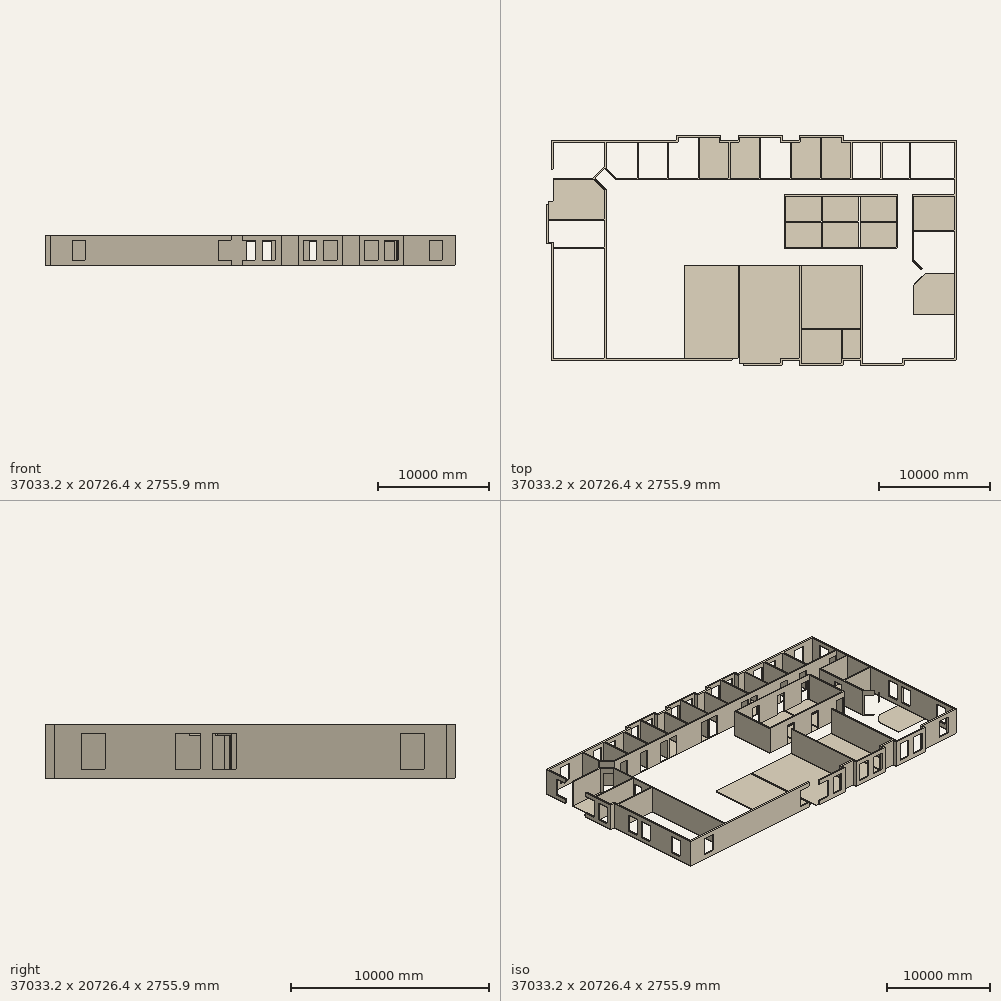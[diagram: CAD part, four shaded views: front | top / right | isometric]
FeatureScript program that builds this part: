
annotation { "Feature Type Name" : "Feature", "Feature Type Description" : "" }
export const myFeature = defineFeature(function(context is Context, id is Id, definition is map)
    precondition{}
    {
        {
            var Q0;
            Q0=qCreatedBy(makeId("Top.planeOp"),FACE);
            var sketch = newSketch(context, id + "F0", { "sketchPlane" : qUnion([Q0])});
            skLineSegment(sketch, "E0", {"start": v(0, 0) * mm, "end": v(11328.4, 0) * mm});
            skLineSegment(sketch, "E1", {"start": v(11328.4, 0) * mm, "end": v(11328.4, 457.2) * mm});
            skLineSegment(sketch, "E2", {"start": v(11328.4, 457.2) * mm, "end": v(15290.8, 457.2) * mm});
            skLineSegment(sketch, "E3", {"start": v(15290.8, 457.2) * mm, "end": v(15290.8, 0) * mm});
            skLineSegment(sketch, "E4", {"start": v(15290.8, 0) * mm, "end": v(16852.9, 0) * mm});
            skLineSegment(sketch, "E5", {"start": v(16852.9, 0) * mm, "end": v(16852.9, 457.2) * mm});
            skLineSegment(sketch, "E6", {"start": v(16852.9, 457.2) * mm, "end": v(20815.3, 457.2) * mm});
            skLineSegment(sketch, "E7", {"start": v(20815.3, 457.2) * mm, "end": v(20815.3, 0) * mm});
            skLineSegment(sketch, "E8", {"start": v(20815.3, 0) * mm, "end": v(22377.4, 0) * mm});
            skLineSegment(sketch, "E9", {"start": v(22377.4, 0) * mm, "end": v(22377.4, 457.2) * mm});
            skLineSegment(sketch, "E10", {"start": v(22377.4, 457.2) * mm, "end": v(26339.8, 457.2) * mm});
            skLineSegment(sketch, "E11", {"start": v(26339.8, 457.2) * mm, "end": v(26339.8, 0) * mm});
            skLineSegment(sketch, "E12", {"start": v(26339.8, 0) * mm, "end": v(36576, 0) * mm});
            skLineSegment(sketch, "E13", {"start": v(0, 0) * mm, "end": v(0, -5330.83) * mm});
            skLineSegment(sketch, "E14", {"start": v(0, -19812) * mm, "end": v(16856.08, -19812) * mm});
            skLineSegment(sketch, "E15", {"start": v(36576, 0) * mm, "end": v(36576, -19812) * mm});
            skLineSegment(sketch, "E16.0", {"start": v(152.4, -152.4) * mm, "end": v(152.4, -5483.23) * mm});
            skLineSegment(sketch, "E16.1", {"start": v(152.4, -19659.6) * mm, "end": v(17008.48, -19659.6) * mm});
            skLineSegment(sketch, "E16.2", {"start": v(36423.6, -152.4) * mm, "end": v(36423.6, -19659.6) * mm});
            skLineSegment(sketch, "E16.3", {"start": v(26187.4, -152.4) * mm, "end": v(36423.6, -152.4) * mm});
            skLineSegment(sketch, "E16.4", {"start": v(26187.4, 304.8) * mm, "end": v(26187.4, -152.4) * mm});
            skLineSegment(sketch, "E16.5", {"start": v(15138.4, -152.4) * mm, "end": v(17005.3, -152.4) * mm});
            skLineSegment(sketch, "E16.6", {"start": v(15138.4, 304.8) * mm, "end": v(15138.4, -152.4) * mm});
            skLineSegment(sketch, "E16.7", {"start": v(11480.8, 304.8) * mm, "end": v(15138.4, 304.8) * mm});
            skLineSegment(sketch, "E16.8", {"start": v(11480.8, -152.4) * mm, "end": v(11480.8, 304.8) * mm});
            skLineSegment(sketch, "E16.9", {"start": v(17005.3, -152.4) * mm, "end": v(17005.3, 304.8) * mm});
            skLineSegment(sketch, "E16.10", {"start": v(17005.3, 304.8) * mm, "end": v(20662.9, 304.8) * mm});
            skLineSegment(sketch, "E16.11", {"start": v(20662.9, 304.8) * mm, "end": v(20662.9, -152.4) * mm});
            skLineSegment(sketch, "E16.12", {"start": v(20662.9, -152.4) * mm, "end": v(22529.8, -152.4) * mm});
            skLineSegment(sketch, "E16.13", {"start": v(22529.8, -152.4) * mm, "end": v(22529.8, 304.8) * mm});
            skLineSegment(sketch, "E16.14", {"start": v(152.4, -152.4) * mm, "end": v(11480.8, -152.4) * mm});
            skLineSegment(sketch, "E16.15", {"start": v(22529.8, 304.8) * mm, "end": v(26187.4, 304.8) * mm});
            skLineSegment(sketch, "E17.bottom", {"start": v(152.4, -3403.6) * mm, "end": v(3762.61, -3403.6) * mm});
            skLineSegment(sketch, "E17.top", {"start": v(152.4, -3517.9) * mm, "end": v(3876.91, -3517.9) * mm});
            skLineSegment(sketch, "E17.left", {"start": v(152.4, -3403.6) * mm, "end": v(152.4, -3517.9) * mm});
            skLineSegment(sketch, "E17.right", {"start": v(36423.6, -3403.6) * mm, "end": v(36423.6, -3517.9) * mm});
            skLineSegment(sketch, "E18", {"start": v(2349.5, 777.7) * mm, "end": v(2349.5, -930.1) * mm, "construction": true});
            skLineSegment(sketch, "E19", {"start": v(6870.7, -930.1) * mm, "end": v(6870.7, 777.7) * mm, "construction": true});
            skLineSegment(sketch, "E20", {"start": v(8699.5, 777.7) * mm, "end": v(8699.5, -930.1) * mm, "construction": true});
            skLineSegment(sketch, "E21", {"start": v(12395.2, 777.7) * mm, "end": v(12395.2, -15.7) * mm, "construction": true});
            skLineSegment(sketch, "E22", {"start": v(14224, -15.7) * mm, "end": v(14224, 777.7) * mm, "construction": true});
            skLineSegment(sketch, "E23", {"start": v(17919.7, 777.7) * mm, "end": v(17919.7, -15.7) * mm, "construction": true});
            skLineSegment(sketch, "E24", {"start": v(19748.5, -15.7) * mm, "end": v(19748.5, 777.7) * mm, "construction": true});
            skLineSegment(sketch, "E25", {"start": v(23444.2, 777.7) * mm, "end": v(23444.2, -15.7) * mm, "construction": true});
            skLineSegment(sketch, "E26", {"start": v(25273, -15.7) * mm, "end": v(25273, 777.7) * mm, "construction": true});
            skLineSegment(sketch, "E27", {"start": v(28895.68, 777.7) * mm, "end": v(28895.68, -930.1) * mm, "construction": true});
            skLineSegment(sketch, "E28", {"start": v(30724.48, -930.1) * mm, "end": v(30724.48, 777.7) * mm, "construction": true});
            skLineSegment(sketch, "E29", {"start": v(34591.63, 777.7) * mm, "end": v(34591.63, -930.1) * mm, "construction": true});
            skPoint(sketch, "E30", {"position": v(8699.5, -76.2) * mm});
            skPoint(sketch, "E31", {"position": v(2349.5, -76.2) * mm});
            skPoint(sketch, "E32", {"position": v(6870.7, -76.2) * mm});
            skPoint(sketch, "E33", {"position": v(28895.68, -76.2) * mm});
            skPoint(sketch, "E34", {"position": v(30724.48, -76.2) * mm});
            skPoint(sketch, "E35", {"position": v(34591.63, -76.2) * mm});
            skPoint(sketch, "E36", {"position": v(23444.2, 381) * mm});
            skPoint(sketch, "E37", {"position": v(25273, 381) * mm});
            skPoint(sketch, "E38", {"position": v(17919.7, 381) * mm});
            skPoint(sketch, "E39", {"position": v(19748.5, 381) * mm});
            skPoint(sketch, "E40", {"position": v(12395.2, 381) * mm});
            skPoint(sketch, "E41", {"position": v(14224, 381) * mm});
            skPoint(sketch, "E42", {"position": v(13309.6, 304.8) * mm});
            skPoint(sketch, "E43", {"position": v(18834.1, 304.8) * mm});
            skPoint(sketch, "E44", {"position": v(24358.6, 304.8) * mm});
            skPoint(sketch, "E45", {"position": v(21596.35, -152.4) * mm});
            skPoint(sketch, "E46", {"position": v(16071.85, -152.4) * mm});
            skPoint(sketch, "E47", {"position": v(29810.08, -152.4) * mm});
            skPoint(sketch, "E48", {"position": v(7785.1, -152.4) * mm});
            skLineSegment(sketch, "E49.bottom", {"start": v(4813.3, -152.4) * mm, "end": v(4927.6, -152.4) * mm});
            skLineSegment(sketch, "E49.left", {"start": v(4813.3, -152.4) * mm, "end": v(4813.3, -2352.91) * mm});
            skLineSegment(sketch, "E49.right", {"start": v(4927.6, -152.4) * mm, "end": v(4927.6, -2467.21) * mm});
            skLineSegment(sketch, "E50.bottom", {"start": v(24301.45, 304.8) * mm, "end": v(24415.75, 304.8) * mm});
            skLineSegment(sketch, "E50.left", {"start": v(24301.45, 304.8) * mm, "end": v(24301.45, -3403.6) * mm});
            skLineSegment(sketch, "E50.right", {"start": v(24415.75, 304.8) * mm, "end": v(24415.75, -3403.6) * mm});
            skLineSegment(sketch, "E51.bottom", {"start": v(18776.95, 304.8) * mm, "end": v(18891.25, 304.8) * mm});
            skLineSegment(sketch, "E51.left", {"start": v(18776.95, 304.8) * mm, "end": v(18776.95, -3403.6) * mm});
            skLineSegment(sketch, "E51.right", {"start": v(18891.25, 304.8) * mm, "end": v(18891.25, -3403.6) * mm});
            skLineSegment(sketch, "E52.bottom", {"start": v(16014.7, -152.4) * mm, "end": v(16129, -152.4) * mm});
            skLineSegment(sketch, "E52.left", {"start": v(16014.7, -152.4) * mm, "end": v(16014.7, -3403.6) * mm});
            skLineSegment(sketch, "E52.right", {"start": v(16129, -152.4) * mm, "end": v(16129, -3403.6) * mm});
            skLineSegment(sketch, "E53.bottom", {"start": v(13252.45, 304.8) * mm, "end": v(13366.75, 304.8) * mm});
            skLineSegment(sketch, "E53.left", {"start": v(13252.45, 304.8) * mm, "end": v(13252.45, -3403.6) * mm});
            skLineSegment(sketch, "E53.right", {"start": v(13366.75, 304.8) * mm, "end": v(13366.75, -3403.6) * mm});
            skLineSegment(sketch, "E54.bottom", {"start": v(7727.95, -152.4) * mm, "end": v(7842.25, -152.4) * mm});
            skLineSegment(sketch, "E54.left", {"start": v(7727.95, -152.4) * mm, "end": v(7727.95, -3403.6) * mm});
            skLineSegment(sketch, "E54.right", {"start": v(7842.25, -152.4) * mm, "end": v(7842.25, -3403.6) * mm});
            skLineSegment(sketch, "E55.bottom", {"start": v(10490.2, -152.4) * mm, "end": v(10604.5, -152.4) * mm});
            skLineSegment(sketch, "E55.left", {"start": v(10490.2, -152.4) * mm, "end": v(10490.2, -3403.6) * mm});
            skLineSegment(sketch, "E55.right", {"start": v(10604.5, -152.4) * mm, "end": v(10604.5, -3403.6) * mm});
            skLineSegment(sketch, "E56.bottom", {"start": v(29752.92, -152.4) * mm, "end": v(29867.23, -152.4) * mm});
            skLineSegment(sketch, "E56.left", {"start": v(29752.92, -152.4) * mm, "end": v(29752.92, -3403.6) * mm});
            skLineSegment(sketch, "E56.right", {"start": v(29867.23, -152.4) * mm, "end": v(29867.23, -3403.6) * mm});
            skLineSegment(sketch, "E57.bottom", {"start": v(21539.2, -152.4) * mm, "end": v(21653.5, -152.4) * mm});
            skLineSegment(sketch, "E57.left", {"start": v(21539.2, -152.4) * mm, "end": v(21539.2, -3403.6) * mm});
            skLineSegment(sketch, "E57.right", {"start": v(21653.5, -152.4) * mm, "end": v(21653.5, -3403.6) * mm});
            skPoint(sketch, "E58", {"position": v(10547.35, -152.4) * mm});
            skPoint(sketch, "E59", {"position": v(27084.34, -152.4) * mm});
            skLineSegment(sketch, "E60.bottom", {"start": v(27027.19, -152.4) * mm, "end": v(27141.49, -152.4) * mm});
            skLineSegment(sketch, "E60.left", {"start": v(27027.19, -152.4) * mm, "end": v(27027.19, -3403.6) * mm});
            skLineSegment(sketch, "E60.right", {"start": v(27141.49, -152.4) * mm, "end": v(27141.49, -3403.6) * mm});
            skLineSegment(sketch, "E61.bottom", {"start": v(11785.6, 457.2) * mm, "end": v(13004.8, 457.2) * mm});
            skLineSegment(sketch, "E61.top", {"start": v(11785.6, 304.8) * mm, "end": v(13004.8, 304.8) * mm});
            skLineSegment(sketch, "E61.left", {"start": v(11785.6, 457.2) * mm, "end": v(11785.6, 304.8) * mm});
            skLineSegment(sketch, "E61.right", {"start": v(13004.8, 457.2) * mm, "end": v(13004.8, 304.8) * mm});
            skLineSegment(sketch, "E62", {"start": v(12395.2, 457.2) * mm, "end": v(12395.2, 304.8) * mm, "construction": true});
            skLineSegment(sketch, "E63.bottom", {"start": v(6261.1, 0) * mm, "end": v(7480.3, 0) * mm});
            skLineSegment(sketch, "E63.top", {"start": v(6261.1, -152.4) * mm, "end": v(7480.3, -152.4) * mm});
            skLineSegment(sketch, "E63.left", {"start": v(6261.1, 0) * mm, "end": v(6261.1, -152.4) * mm});
            skLineSegment(sketch, "E63.right", {"start": v(7480.3, 0) * mm, "end": v(7480.3, -152.4) * mm});
            skLineSegment(sketch, "E64", {"start": v(6870.7, 0) * mm, "end": v(6870.7, -152.4) * mm, "construction": true});
            skLineSegment(sketch, "E65.bottom", {"start": v(8089.9, 0) * mm, "end": v(9309.1, 0) * mm});
            skLineSegment(sketch, "E65.top", {"start": v(8089.9, -152.4) * mm, "end": v(9309.1, -152.4) * mm});
            skLineSegment(sketch, "E65.left", {"start": v(8089.9, 0) * mm, "end": v(8089.9, -152.4) * mm});
            skLineSegment(sketch, "E65.right", {"start": v(9309.1, 0) * mm, "end": v(9309.1, -152.4) * mm});
            skLineSegment(sketch, "E66", {"start": v(8699.5, 0) * mm, "end": v(8699.5, -152.4) * mm, "construction": true});
            skLineSegment(sketch, "E67.bottom", {"start": v(1739.9, 0) * mm, "end": v(2959.1, 0) * mm});
            skLineSegment(sketch, "E67.top", {"start": v(1739.9, -152.4) * mm, "end": v(2959.1, -152.4) * mm});
            skLineSegment(sketch, "E67.left", {"start": v(1739.9, 0) * mm, "end": v(1739.9, -152.4) * mm});
            skLineSegment(sketch, "E67.right", {"start": v(2959.1, 0) * mm, "end": v(2959.1, -152.4) * mm});
            skLineSegment(sketch, "E68", {"start": v(2349.5, 0) * mm, "end": v(2349.5, -152.4) * mm, "construction": true});
            skLineSegment(sketch, "E69.bottom", {"start": v(13614.4, 457.2) * mm, "end": v(14833.6, 457.2) * mm});
            skLineSegment(sketch, "E69.top", {"start": v(13614.4, 304.8) * mm, "end": v(14833.6, 304.8) * mm});
            skLineSegment(sketch, "E69.left", {"start": v(13614.4, 457.2) * mm, "end": v(13614.4, 304.8) * mm});
            skLineSegment(sketch, "E69.right", {"start": v(14833.6, 457.2) * mm, "end": v(14833.6, 304.8) * mm});
            skLineSegment(sketch, "E70", {"start": v(14224, 457.2) * mm, "end": v(14224, 304.8) * mm, "construction": true});
            skLineSegment(sketch, "E71.bottom", {"start": v(17310.1, 457.2) * mm, "end": v(18529.3, 457.2) * mm});
            skLineSegment(sketch, "E71.top", {"start": v(17310.1, 304.8) * mm, "end": v(18529.3, 304.8) * mm});
            skLineSegment(sketch, "E71.left", {"start": v(17310.1, 457.2) * mm, "end": v(17310.1, 304.8) * mm});
            skLineSegment(sketch, "E71.right", {"start": v(18529.3, 457.2) * mm, "end": v(18529.3, 304.8) * mm});
            skLineSegment(sketch, "E72", {"start": v(17919.7, 457.2) * mm, "end": v(17919.7, 304.8) * mm, "construction": true});
            skLineSegment(sketch, "E73.bottom", {"start": v(19138.9, 457.2) * mm, "end": v(20358.1, 457.2) * mm});
            skLineSegment(sketch, "E73.top", {"start": v(19138.9, 304.8) * mm, "end": v(20358.1, 304.8) * mm});
            skLineSegment(sketch, "E73.left", {"start": v(19138.9, 457.2) * mm, "end": v(19138.9, 304.8) * mm});
            skLineSegment(sketch, "E73.right", {"start": v(20358.1, 457.2) * mm, "end": v(20358.1, 304.8) * mm});
            skLineSegment(sketch, "E74", {"start": v(19748.5, 457.2) * mm, "end": v(19748.5, 304.8) * mm, "construction": true});
            skLineSegment(sketch, "E75.bottom", {"start": v(22834.6, 457.2) * mm, "end": v(24053.8, 457.2) * mm});
            skLineSegment(sketch, "E75.top", {"start": v(22834.6, 304.8) * mm, "end": v(24053.8, 304.8) * mm});
            skLineSegment(sketch, "E75.left", {"start": v(22834.6, 457.2) * mm, "end": v(22834.6, 304.8) * mm});
            skLineSegment(sketch, "E75.right", {"start": v(24053.8, 457.2) * mm, "end": v(24053.8, 304.8) * mm});
            skLineSegment(sketch, "E76", {"start": v(23444.2, 457.2) * mm, "end": v(23444.2, 304.8) * mm, "construction": true});
            skLineSegment(sketch, "E77.bottom", {"start": v(24663.4, 457.2) * mm, "end": v(25882.6, 457.2) * mm});
            skLineSegment(sketch, "E77.top", {"start": v(24663.4, 304.8) * mm, "end": v(25882.6, 304.8) * mm});
            skLineSegment(sketch, "E77.left", {"start": v(24663.4, 457.2) * mm, "end": v(24663.4, 304.8) * mm});
            skLineSegment(sketch, "E77.right", {"start": v(25882.6, 457.2) * mm, "end": v(25882.6, 304.8) * mm});
            skLineSegment(sketch, "E78", {"start": v(25273, 457.2) * mm, "end": v(25273, 304.8) * mm, "construction": true});
            skLineSegment(sketch, "E79.bottom", {"start": v(-457.2, -7007.23) * mm, "end": v(-457.2, -5788.03) * mm});
            skLineSegment(sketch, "E79.top", {"start": v(-304.8, -7007.23) * mm, "end": v(-304.8, -5788.03) * mm});
            skLineSegment(sketch, "E79.left", {"start": v(-457.2, -7007.23) * mm, "end": v(-304.8, -7007.23) * mm});
            skLineSegment(sketch, "E79.right", {"start": v(-457.2, -5788.03) * mm, "end": v(-304.8, -5788.03) * mm});
            skLineSegment(sketch, "E80", {"start": v(-457.2, -6397.63) * mm, "end": v(-304.8, -6397.63) * mm, "construction": true});
            skPoint(sketch, "E81", {"position": v(-381, -6397.63) * mm});
            skLineSegment(sketch, "E82.bottom", {"start": v(33982.03, 0) * mm, "end": v(35201.23, 0) * mm});
            skLineSegment(sketch, "E82.top", {"start": v(33982.03, -152.4) * mm, "end": v(35201.23, -152.4) * mm});
            skLineSegment(sketch, "E82.left", {"start": v(33982.03, 0) * mm, "end": v(33982.03, -152.4) * mm});
            skLineSegment(sketch, "E82.right", {"start": v(35201.23, 0) * mm, "end": v(35201.23, -152.4) * mm});
            skLineSegment(sketch, "E83", {"start": v(34591.63, 0) * mm, "end": v(34591.63, -152.4) * mm, "construction": true});
            skLineSegment(sketch, "E84.bottom", {"start": v(30114.88, 0) * mm, "end": v(31334.08, 0) * mm});
            skLineSegment(sketch, "E84.top", {"start": v(30114.87, -152.4) * mm, "end": v(31334.08, -152.4) * mm});
            skLineSegment(sketch, "E84.left", {"start": v(30114.88, 0) * mm, "end": v(30114.88, -152.4) * mm});
            skLineSegment(sketch, "E84.right", {"start": v(31334.08, 0) * mm, "end": v(31334.08, -152.4) * mm});
            skLineSegment(sketch, "E85", {"start": v(30724.48, 0) * mm, "end": v(30724.48, -152.4) * mm, "construction": true});
            skLineSegment(sketch, "E86.bottom", {"start": v(28286.08, 0) * mm, "end": v(29505.28, 0) * mm});
            skLineSegment(sketch, "E86.top", {"start": v(28286.08, -152.4) * mm, "end": v(29505.28, -152.4) * mm});
            skLineSegment(sketch, "E86.left", {"start": v(28286.08, 0) * mm, "end": v(28286.08, -152.4) * mm});
            skLineSegment(sketch, "E86.right", {"start": v(29505.28, 0) * mm, "end": v(29505.28, -152.4) * mm});
            skLineSegment(sketch, "E87", {"start": v(28895.68, 0) * mm, "end": v(28895.68, -152.4) * mm, "construction": true});
            skPoint(sketch, "E88", {"position": v(4870.45, -152.4) * mm});
            skPoint(sketch, "E89", {"position": v(32362.78, -152.4) * mm});
            skLineSegment(sketch, "E90.bottom", {"start": v(32305.63, -152.4) * mm, "end": v(32419.93, -152.4) * mm});
            skLineSegment(sketch, "E90.left", {"start": v(32305.63, -152.4) * mm, "end": v(32305.63, -3403.6) * mm});
            skLineSegment(sketch, "E90.right", {"start": v(32419.93, -152.4) * mm, "end": v(32419.93, -3403.6) * mm});
            skLineSegment(sketch, "E91", {"start": v(4927.6, -4406.95) * mm, "end": v(3924.25, -3403.6) * mm});
            skLineSegment(sketch, "E92", {"start": v(5863.99, -3403.6) * mm, "end": v(4927.6, -2467.21) * mm});
            skLineSegment(sketch, "E93", {"start": v(5816.65, -3517.9) * mm, "end": v(4813.3, -2514.55) * mm});
            skLineSegment(sketch, "E94", {"start": v(4813.3, -4454.29) * mm, "end": v(3876.91, -3517.9) * mm});
            skLineSegment(sketch, "E95", {"start": v(3924.25, -3403.6) * mm, "end": v(4813.3, -2514.55) * mm});
            skLineSegment(sketch, "E96", {"start": v(3762.61, -3403.6) * mm, "end": v(4813.3, -2352.91) * mm});
            skLineSegment(sketch, "E97.trimOffspring", {"start": v(5863.99, -3403.6) * mm, "end": v(36423.6, -3403.6) * mm});
            skLineSegment(sketch, "E98.trimOffspring", {"start": v(5816.65, -3517.9) * mm, "end": v(36423.6, -3517.9) * mm});
            skLineSegment(sketch, "E99.trimOffspring", {"start": v(4813.3, -4454.29) * mm, "end": v(4813.3, -19659.6) * mm});
            skLineSegment(sketch, "E100.trimOffspring", {"start": v(4927.6, -4406.95) * mm, "end": v(4927.6, -19659.6) * mm});
            skLineSegment(sketch, "E101", {"start": v(-1433.95, -6397.63) * mm, "end": v(671.95, -6397.63) * mm, "construction": true});
            skPoint(sketch, "E102", {"position": v(76.2, -1968.5) * mm});
            skLineSegment(sketch, "E103.bottom", {"start": v(0, -14322.43) * mm, "end": v(0, -13103.23) * mm});
            skLineSegment(sketch, "E103.top", {"start": v(152.4, -14322.43) * mm, "end": v(152.4, -13103.23) * mm});
            skLineSegment(sketch, "E103.left", {"start": v(0, -14322.43) * mm, "end": v(152.4, -14322.43) * mm});
            skLineSegment(sketch, "E103.right", {"start": v(0, -13103.23) * mm, "end": v(152.4, -13103.23) * mm});
            skLineSegment(sketch, "E104", {"start": v(0, -13712.83) * mm, "end": v(152.4, -13712.83) * mm, "construction": true});
            skPoint(sketch, "E105", {"position": v(76.2, -13712.83) * mm});
            skLineSegment(sketch, "E106", {"start": v(-603.17, -13712.83) * mm, "end": v(755.57, -13712.83) * mm, "construction": true});
            skLineSegment(sketch, "E107.bottom", {"start": v(0, -12493.63) * mm, "end": v(0, -11274.43) * mm});
            skLineSegment(sketch, "E107.top", {"start": v(152.4, -12493.63) * mm, "end": v(152.4, -11274.43) * mm});
            skLineSegment(sketch, "E107.left", {"start": v(0, -12493.63) * mm, "end": v(152.4, -12493.63) * mm});
            skLineSegment(sketch, "E107.right", {"start": v(0, -11274.43) * mm, "end": v(152.4, -11274.43) * mm});
            skLineSegment(sketch, "E108", {"start": v(0, -11884.03) * mm, "end": v(152.4, -11884.03) * mm, "construction": true});
            skPoint(sketch, "E109", {"position": v(76.2, -11884.03) * mm});
            skLineSegment(sketch, "E110", {"start": v(-593.94, -11884.03) * mm, "end": v(746.34, -11884.03) * mm, "construction": true});
            skLineSegment(sketch, "E111.bottom", {"start": v(0, -2578.1) * mm, "end": v(0, -1358.9) * mm});
            skLineSegment(sketch, "E111.top", {"start": v(152.4, -2578.1) * mm, "end": v(152.4, -1358.9) * mm});
            skLineSegment(sketch, "E111.left", {"start": v(0, -2578.1) * mm, "end": v(152.4, -2578.1) * mm});
            skLineSegment(sketch, "E111.right", {"start": v(0, -1358.9) * mm, "end": v(152.4, -1358.9) * mm});
            skLineSegment(sketch, "E112", {"start": v(0, -1968.5) * mm, "end": v(152.4, -1968.5) * mm, "construction": true});
            skLineSegment(sketch, "E113", {"start": v(-519.55, -1968.5) * mm, "end": v(671.95, -1968.5) * mm, "construction": true});
            skLineSegment(sketch, "E114.bottom", {"start": v(0, -18453.1) * mm, "end": v(0, -17233.9) * mm});
            skLineSegment(sketch, "E114.top", {"start": v(152.4, -18453.1) * mm, "end": v(152.4, -17233.9) * mm});
            skLineSegment(sketch, "E114.left", {"start": v(0, -18453.1) * mm, "end": v(152.4, -18453.1) * mm});
            skLineSegment(sketch, "E114.right", {"start": v(0, -17233.9) * mm, "end": v(152.4, -17233.9) * mm});
            skLineSegment(sketch, "E115", {"start": v(0, -17843.5) * mm, "end": v(152.4, -17843.5) * mm, "construction": true});
            skPoint(sketch, "E116", {"position": v(76.2, -17843.5) * mm});
            skLineSegment(sketch, "E117", {"start": v(-617.62, -17843.5) * mm, "end": v(770.02, -17843.5) * mm, "construction": true});
            skLineSegment(sketch, "E118.bottom", {"start": v(-457.2, -8836.03) * mm, "end": v(-457.2, -7616.83) * mm});
            skLineSegment(sketch, "E118.top", {"start": v(-304.8, -8836.03) * mm, "end": v(-304.8, -7616.83) * mm});
            skLineSegment(sketch, "E118.left", {"start": v(-457.2, -8836.03) * mm, "end": v(-304.8, -8836.03) * mm});
            skLineSegment(sketch, "E118.right", {"start": v(-457.2, -7616.83) * mm, "end": v(-304.8, -7616.83) * mm});
            skLineSegment(sketch, "E119", {"start": v(-457.2, -8226.43) * mm, "end": v(-304.8, -8226.43) * mm, "construction": true});
            skPoint(sketch, "E120", {"position": v(-381, -8226.43) * mm});
            skLineSegment(sketch, "E121", {"start": v(-1375.04, -8226.43) * mm, "end": v(613.04, -8226.43) * mm, "construction": true});
            skLineSegment(sketch, "E122", {"start": v(4813.3, -7064.38) * mm, "end": v(-304.8, -7064.38) * mm});
            skLineSegment(sketch, "E123", {"start": v(-304.8, -7064.38) * mm, "end": v(-304.8, -7178.68) * mm});
            skLineSegment(sketch, "E124", {"start": v(-304.8, -7178.68) * mm, "end": v(4813.3, -7178.68) * mm});
            skLineSegment(sketch, "E125.bottom", {"start": v(-457.2, -5330.83) * mm, "end": v(0, -5330.83) * mm});
            skLineSegment(sketch, "E125.top", {"start": v(-457.2, -9293.23) * mm, "end": v(0, -9293.23) * mm});
            skLineSegment(sketch, "E126.1", {"start": v(-304.8, -5483.23) * mm, "end": v(152.4, -5483.23) * mm});
            skLineSegment(sketch, "E126.3", {"start": v(-304.8, -9140.83) * mm, "end": v(152.4, -9140.83) * mm});
            skLineSegment(sketch, "E127.trimOffspring", {"start": v(0, -9293.23) * mm, "end": v(0, -19812) * mm});
            skLineSegment(sketch, "E128.trimOffspring", {"start": v(152.4, -9140.83) * mm, "end": v(152.4, -19659.6) * mm});
            skLineSegment(sketch, "E129", {"start": v(-457.2, -5330.83) * mm, "end": v(-457.2, -9293.23) * mm});
            skLineSegment(sketch, "E130", {"start": v(-304.8, -5483.23) * mm, "end": v(-304.8, -9140.83) * mm});
            skPoint(sketch, "E131", {"position": v(-304.8, -7121.53) * mm});
            skPoint(sketch, "E132", {"position": v(152.4, -9674.23) * mm});
            skLineSegment(sketch, "E133", {"start": v(4813.3, -9617.08) * mm, "end": v(152.4, -9617.08) * mm});
            skLineSegment(sketch, "E134", {"start": v(152.4, -9617.08) * mm, "end": v(152.4, -9731.38) * mm});
            skLineSegment(sketch, "E135", {"start": v(152.4, -9731.38) * mm, "end": v(4813.3, -9731.38) * mm});
            skLineSegment(sketch, "E136.bottom", {"start": v(32734.25, -5003.8) * mm, "end": v(36423.6, -5003.8) * mm});
            skLineSegment(sketch, "E136.top", {"start": v(32734.25, -8083.55) * mm, "end": v(36423.6, -8083.55) * mm});
            skLineSegment(sketch, "E136.left", {"start": v(32734.25, -5003.8) * mm, "end": v(32734.25, -10845.8) * mm});
            skLineSegment(sketch, "E136.right", {"start": v(36423.6, -5003.8) * mm, "end": v(36423.6, -8083.55) * mm});
            skLineSegment(sketch, "E137.1", {"start": v(32619.95, -4889.5) * mm, "end": v(36423.6, -4889.5) * mm});
            skLineSegment(sketch, "E137.2", {"start": v(32619.95, -4889.5) * mm, "end": v(32619.95, -10893.14) * mm});
            skLineSegment(sketch, "E137.3", {"start": v(32734.25, -8197.85) * mm, "end": v(36423.6, -8197.85) * mm});
            skLineSegment(sketch, "E138.bottom", {"start": v(31248.35, -4889.5) * mm, "end": v(21028.03, -4889.5) * mm});
            skLineSegment(sketch, "E138.top", {"start": v(31248.35, -9747.25) * mm, "end": v(21028.03, -9747.25) * mm});
            skLineSegment(sketch, "E138.left", {"start": v(31248.35, -4889.5) * mm, "end": v(31248.35, -9747.25) * mm});
            skLineSegment(sketch, "E138.right", {"start": v(21028.03, -4889.5) * mm, "end": v(21028.03, -9747.25) * mm});
            skLineSegment(sketch, "E139.0", {"start": v(31134.05, -5003.8) * mm, "end": v(21142.33, -5003.8) * mm});
            skLineSegment(sketch, "E139.1", {"start": v(31134.05, -5003.8) * mm, "end": v(31134.05, -9632.95) * mm});
            skLineSegment(sketch, "E139.2", {"start": v(31134.05, -9632.95) * mm, "end": v(21142.33, -9632.95) * mm});
            skLineSegment(sketch, "E139.3", {"start": v(21142.33, -5003.8) * mm, "end": v(21142.33, -9632.95) * mm});
            skLineSegment(sketch, "E140", {"start": v(21142.33, -7261.23) * mm, "end": v(24396.7, -7261.23) * mm});
            skLineSegment(sketch, "E141", {"start": v(21142.33, -7375.53) * mm, "end": v(24396.7, -7375.53) * mm});
            skLineSegment(sketch, "E142", {"start": v(24396.7, -5003.8) * mm, "end": v(24396.7, -7261.23) * mm});
            skLineSegment(sketch, "E143", {"start": v(24511, -9632.95) * mm, "end": v(24511, -7375.53) * mm});
            skLineSegment(sketch, "E144", {"start": v(27765.38, -5003.8) * mm, "end": v(27765.38, -7261.23) * mm});
            skLineSegment(sketch, "E145", {"start": v(27879.68, -9632.95) * mm, "end": v(27879.68, -7375.53) * mm});
            skLineSegment(sketch, "E146.trimOffspring", {"start": v(24511, -7261.23) * mm, "end": v(27765.38, -7261.23) * mm});
            skLineSegment(sketch, "E147.trimOffspring", {"start": v(24511, -7375.53) * mm, "end": v(27765.38, -7375.53) * mm});
            skLineSegment(sketch, "E148.trimOffspring", {"start": v(24511, -7261.23) * mm, "end": v(24511, -5003.8) * mm});
            skLineSegment(sketch, "E149.trimOffspring", {"start": v(24396.7, -7375.53) * mm, "end": v(24396.7, -9632.95) * mm});
            skLineSegment(sketch, "E150.trimOffspring", {"start": v(27765.38, -7375.53) * mm, "end": v(27765.38, -9632.95) * mm});
            skLineSegment(sketch, "E151.trimOffspring", {"start": v(27879.68, -7261.23) * mm, "end": v(27879.68, -5003.8) * mm});
            skLineSegment(sketch, "E152.trimOffspring", {"start": v(27879.68, -7375.53) * mm, "end": v(31134.05, -7375.53) * mm});
            skLineSegment(sketch, "E153.trimOffspring", {"start": v(27879.68, -7261.23) * mm, "end": v(31134.05, -7261.23) * mm});
            skLineSegment(sketch, "E154.bottom", {"start": v(36423.6, -2336.8) * mm, "end": v(36423.6, -1117.6) * mm});
            skLineSegment(sketch, "E154.top", {"start": v(36576, -2336.8) * mm, "end": v(36576, -1117.6) * mm});
            skLineSegment(sketch, "E154.left", {"start": v(36423.6, -2336.8) * mm, "end": v(36576, -2336.8) * mm});
            skLineSegment(sketch, "E154.right", {"start": v(36423.6, -1117.6) * mm, "end": v(36576, -1117.6) * mm});
            skLineSegment(sketch, "E155", {"start": v(36423.6, -1727.2) * mm, "end": v(36576, -1727.2) * mm, "construction": true});
            skPoint(sketch, "E156", {"position": v(36499.8, -1727.2) * mm});
            skLineSegment(sketch, "E157", {"start": v(35659.18, -1727.2) * mm, "end": v(37340.42, -1727.2) * mm, "construction": true});
            skLineSegment(sketch, "E158.bottom", {"start": v(36423.6, -11849.1) * mm, "end": v(36423.6, -10629.9) * mm});
            skLineSegment(sketch, "E158.top", {"start": v(36576, -11849.1) * mm, "end": v(36576, -10629.9) * mm});
            skLineSegment(sketch, "E158.left", {"start": v(36423.6, -11849.1) * mm, "end": v(36576, -11849.1) * mm});
            skLineSegment(sketch, "E158.right", {"start": v(36423.6, -10629.9) * mm, "end": v(36576, -10629.9) * mm});
            skLineSegment(sketch, "E159", {"start": v(36423.6, -11239.5) * mm, "end": v(36576, -11239.5) * mm, "construction": true});
            skPoint(sketch, "E160", {"position": v(36499.8, -11239.5) * mm});
            skLineSegment(sketch, "E161", {"start": v(35812.04, -11239.5) * mm, "end": v(37187.56, -11239.5) * mm, "construction": true});
            skLineSegment(sketch, "E162.bottom", {"start": v(36423.6, -13677.9) * mm, "end": v(36423.6, -12458.7) * mm});
            skLineSegment(sketch, "E162.top", {"start": v(36576, -13677.9) * mm, "end": v(36576, -12458.7) * mm});
            skLineSegment(sketch, "E162.left", {"start": v(36423.6, -13677.9) * mm, "end": v(36576, -13677.9) * mm});
            skLineSegment(sketch, "E162.right", {"start": v(36423.6, -12458.7) * mm, "end": v(36576, -12458.7) * mm});
            skLineSegment(sketch, "E163", {"start": v(36423.6, -13068.3) * mm, "end": v(36576, -13068.3) * mm, "construction": true});
            skPoint(sketch, "E164", {"position": v(36499.8, -13068.3) * mm});
            skLineSegment(sketch, "E165", {"start": v(35750.9, -13068.3) * mm, "end": v(37248.7, -13068.3) * mm, "construction": true});
            skLineSegment(sketch, "E166.bottom", {"start": v(36423.6, -18453.1) * mm, "end": v(36423.6, -17233.9) * mm});
            skLineSegment(sketch, "E166.top", {"start": v(36576, -18453.1) * mm, "end": v(36576, -17233.9) * mm});
            skLineSegment(sketch, "E166.left", {"start": v(36423.6, -18453.1) * mm, "end": v(36576, -18453.1) * mm});
            skLineSegment(sketch, "E166.right", {"start": v(36423.6, -17233.9) * mm, "end": v(36576, -17233.9) * mm});
            skLineSegment(sketch, "E167", {"start": v(36423.6, -17843.5) * mm, "end": v(36576, -17843.5) * mm, "construction": true});
            skPoint(sketch, "E168", {"position": v(36499.8, -17843.5) * mm});
            skLineSegment(sketch, "E169", {"start": v(35689.76, -17843.5) * mm, "end": v(37309.84, -17843.5) * mm, "construction": true});
            skLineSegment(sketch, "E170", {"start": v(36423.6, -11906.25) * mm, "end": v(36423.6, -12020.55) * mm});
            skLineSegment(sketch, "E171", {"start": v(36423.6, -11849.1) * mm, "end": v(36423.6, -12458.7) * mm});
            skPoint(sketch, "E172", {"position": v(36423.6, -11963.4) * mm});
            skPoint(sketch, "E173", {"position": v(36423.6, -12153.9) * mm});
            skLineSegment(sketch, "E174", {"start": v(30905.92, -11118.85) * mm, "end": v(11918.95, -11118.85) * mm});
            skLineSegment(sketch, "E175", {"start": v(12033.25, -11233.15) * mm, "end": v(16894.18, -11233.15) * mm});
            skLineSegment(sketch, "E176", {"start": v(31867.48, -19812) * mm, "end": v(31867.48, -20269.2) * mm});
            skLineSegment(sketch, "E177", {"start": v(31867.48, -20269.2) * mm, "end": v(27905.08, -20269.2) * mm});
            skLineSegment(sketch, "E178", {"start": v(27905.08, -20269.2) * mm, "end": v(27905.08, -19812) * mm});
            skLineSegment(sketch, "E179", {"start": v(31715.08, -19659.6) * mm, "end": v(31715.08, -20116.8) * mm});
            skLineSegment(sketch, "E180", {"start": v(31715.08, -20116.8) * mm, "end": v(28057.48, -20116.8) * mm});
            skLineSegment(sketch, "E181", {"start": v(28057.48, -20116.8) * mm, "end": v(28057.48, -19659.6) * mm});
            skLineSegment(sketch, "E182", {"start": v(26342.98, -19812) * mm, "end": v(26342.98, -20269.2) * mm});
            skLineSegment(sketch, "E183", {"start": v(26342.98, -20269.2) * mm, "end": v(22380.58, -20269.2) * mm});
            skLineSegment(sketch, "E184", {"start": v(22380.58, -20269.2) * mm, "end": v(22380.58, -19812) * mm});
            skLineSegment(sketch, "E185", {"start": v(26190.58, -19659.6) * mm, "end": v(26190.58, -20116.8) * mm});
            skLineSegment(sketch, "E186", {"start": v(26190.58, -20116.8) * mm, "end": v(22532.98, -20116.8) * mm});
            skLineSegment(sketch, "E187", {"start": v(22532.98, -20116.8) * mm, "end": v(22532.98, -19659.6) * mm});
            skLineSegment(sketch, "E188", {"start": v(20818.48, -19812) * mm, "end": v(20818.48, -20269.2) * mm});
            skLineSegment(sketch, "E189", {"start": v(20818.48, -20269.2) * mm, "end": v(16856.08, -20269.2) * mm});
            skLineSegment(sketch, "E190", {"start": v(16856.08, -20269.2) * mm, "end": v(16856.08, -19812) * mm});
            skLineSegment(sketch, "E191", {"start": v(20666.08, -19659.6) * mm, "end": v(20666.08, -20116.8) * mm});
            skLineSegment(sketch, "E192", {"start": v(20666.08, -20116.8) * mm, "end": v(17008.48, -20116.8) * mm});
            skLineSegment(sketch, "E193", {"start": v(17008.48, -20116.8) * mm, "end": v(17008.48, -19659.6) * mm});
            skLineSegment(sketch, "E194", {"start": v(20818.48, -19812) * mm, "end": v(22380.58, -19812) * mm});
            skLineSegment(sketch, "E195", {"start": v(20666.08, -19659.6) * mm, "end": v(22532.98, -19659.6) * mm});
            skLineSegment(sketch, "E196", {"start": v(26342.98, -19812) * mm, "end": v(27905.08, -19812) * mm});
            skLineSegment(sketch, "E197", {"start": v(26190.58, -19659.6) * mm, "end": v(28057.48, -19659.6) * mm});
            skLineSegment(sketch, "E198", {"start": v(23447.38, -19543.06) * mm, "end": v(23447.38, -20842.94) * mm, "construction": true});
            skLineSegment(sketch, "E199", {"start": v(25276.18, -20842.94) * mm, "end": v(25276.18, -19543.06) * mm, "construction": true});
            skPoint(sketch, "E200", {"position": v(23447.38, -20193) * mm});
            skPoint(sketch, "E201", {"position": v(25276.18, -20193) * mm});
            skLineSegment(sketch, "E202.bottom", {"start": v(22837.78, -20116.8) * mm, "end": v(24056.98, -20116.8) * mm});
            skLineSegment(sketch, "E202.top", {"start": v(22837.78, -20269.2) * mm, "end": v(24056.98, -20269.2) * mm});
            skLineSegment(sketch, "E202.left", {"start": v(22837.78, -20116.8) * mm, "end": v(22837.78, -20269.2) * mm});
            skLineSegment(sketch, "E202.right", {"start": v(24056.98, -20116.8) * mm, "end": v(24056.98, -20269.2) * mm});
            skLineSegment(sketch, "E203", {"start": v(23447.38, -20116.8) * mm, "end": v(23447.38, -20269.2) * mm, "construction": true});
            skLineSegment(sketch, "E204.bottom", {"start": v(24666.58, -20116.8) * mm, "end": v(25885.78, -20116.8) * mm});
            skLineSegment(sketch, "E204.top", {"start": v(24666.58, -20269.2) * mm, "end": v(25885.78, -20269.2) * mm});
            skLineSegment(sketch, "E204.left", {"start": v(24666.58, -20116.8) * mm, "end": v(24666.58, -20269.2) * mm});
            skLineSegment(sketch, "E204.right", {"start": v(25885.78, -20116.8) * mm, "end": v(25885.78, -20269.2) * mm});
            skLineSegment(sketch, "E205", {"start": v(25276.18, -20116.8) * mm, "end": v(25276.18, -20269.2) * mm, "construction": true});
            skPoint(sketch, "E206", {"position": v(24361.78, -20193) * mm});
            skPoint(sketch, "E207", {"position": v(29886.28, -20193) * mm});
            skPoint(sketch, "E208", {"position": v(18837.28, -20193) * mm});
            skLineSegment(sketch, "E209", {"start": v(17922.88, -19558.35) * mm, "end": v(17922.88, -20827.65) * mm, "construction": true});
            skLineSegment(sketch, "E210", {"start": v(19751.68, -20827.65) * mm, "end": v(19751.68, -19558.35) * mm, "construction": true});
            skPoint(sketch, "E211", {"position": v(17922.88, -20193) * mm});
            skPoint(sketch, "E212", {"position": v(19751.68, -20193) * mm});
            skLineSegment(sketch, "E213.bottom", {"start": v(17313.28, -20116.8) * mm, "end": v(18532.48, -20116.8) * mm});
            skLineSegment(sketch, "E213.top", {"start": v(17313.28, -20269.2) * mm, "end": v(18532.48, -20269.2) * mm});
            skLineSegment(sketch, "E213.left", {"start": v(17313.28, -20116.8) * mm, "end": v(17313.28, -20269.2) * mm});
            skLineSegment(sketch, "E213.right", {"start": v(18532.48, -20116.8) * mm, "end": v(18532.48, -20269.2) * mm});
            skLineSegment(sketch, "E214", {"start": v(17922.88, -20116.8) * mm, "end": v(17922.88, -20269.2) * mm, "construction": true});
            skLineSegment(sketch, "E215.bottom", {"start": v(19142.08, -20116.8) * mm, "end": v(20361.28, -20116.8) * mm});
            skLineSegment(sketch, "E215.top", {"start": v(19142.08, -20269.2) * mm, "end": v(20361.28, -20269.2) * mm});
            skLineSegment(sketch, "E215.left", {"start": v(19142.08, -20116.8) * mm, "end": v(19142.08, -20269.2) * mm});
            skLineSegment(sketch, "E215.right", {"start": v(20361.28, -20116.8) * mm, "end": v(20361.28, -20269.2) * mm});
            skLineSegment(sketch, "E216", {"start": v(19751.68, -20116.8) * mm, "end": v(19751.68, -20269.2) * mm, "construction": true});
            skLineSegment(sketch, "E217", {"start": v(28971.88, -19344.36) * mm, "end": v(28971.88, -21041.64) * mm, "construction": true});
            skLineSegment(sketch, "E218", {"start": v(30800.68, -21041.64) * mm, "end": v(30800.68, -19344.36) * mm, "construction": true});
            skPoint(sketch, "E219", {"position": v(28971.88, -20193) * mm});
            skPoint(sketch, "E220", {"position": v(30800.68, -20193) * mm});
            skLineSegment(sketch, "E221.bottom", {"start": v(28362.28, -20116.8) * mm, "end": v(29581.48, -20116.8) * mm});
            skLineSegment(sketch, "E221.top", {"start": v(28362.28, -20269.2) * mm, "end": v(29581.48, -20269.2) * mm});
            skLineSegment(sketch, "E221.left", {"start": v(28362.28, -20116.8) * mm, "end": v(28362.28, -20269.2) * mm});
            skLineSegment(sketch, "E221.right", {"start": v(29581.48, -20116.8) * mm, "end": v(29581.48, -20269.2) * mm});
            skLineSegment(sketch, "E222", {"start": v(28971.88, -20116.8) * mm, "end": v(28971.88, -20269.2) * mm, "construction": true});
            skLineSegment(sketch, "E223.bottom", {"start": v(30191.08, -20116.8) * mm, "end": v(31410.28, -20116.8) * mm});
            skLineSegment(sketch, "E223.top", {"start": v(30191.08, -20269.2) * mm, "end": v(31410.28, -20269.2) * mm});
            skLineSegment(sketch, "E223.left", {"start": v(30191.08, -20116.8) * mm, "end": v(30191.08, -20269.2) * mm});
            skLineSegment(sketch, "E223.right", {"start": v(31410.28, -20116.8) * mm, "end": v(31410.28, -20269.2) * mm});
            skLineSegment(sketch, "E224", {"start": v(30800.68, -20116.8) * mm, "end": v(30800.68, -20269.2) * mm, "construction": true});
            skLineSegment(sketch, "E225.trimOffspring", {"start": v(31867.48, -19812) * mm, "end": v(36576, -19812) * mm});
            skLineSegment(sketch, "E226.trimOffspring", {"start": v(31715.08, -19659.6) * mm, "end": v(36423.6, -19659.6) * mm});
            skPoint(sketch, "E227", {"position": v(34810.7, -19735.8) * mm});
            skLineSegment(sketch, "E228.bottom", {"start": v(34201.1, -19659.6) * mm, "end": v(35420.3, -19659.6) * mm});
            skLineSegment(sketch, "E228.top", {"start": v(34201.1, -19812) * mm, "end": v(35420.3, -19812) * mm});
            skLineSegment(sketch, "E228.left", {"start": v(34201.1, -19659.6) * mm, "end": v(34201.1, -19812) * mm});
            skLineSegment(sketch, "E228.right", {"start": v(35420.3, -19659.6) * mm, "end": v(35420.3, -19812) * mm});
            skLineSegment(sketch, "E229", {"start": v(34810.7, -19659.6) * mm, "end": v(34810.7, -19812) * mm, "construction": true});
            skPoint(sketch, "E230", {"position": v(15738.48, -19735.8) * mm});
            skLineSegment(sketch, "E231.bottom", {"start": v(15128.88, -19659.6) * mm, "end": v(16348.08, -19659.6) * mm});
            skLineSegment(sketch, "E231.top", {"start": v(15128.87, -19812) * mm, "end": v(16348.08, -19812) * mm});
            skLineSegment(sketch, "E231.left", {"start": v(15128.87, -19659.6) * mm, "end": v(15128.87, -19812) * mm});
            skLineSegment(sketch, "E231.right", {"start": v(16348.08, -19659.6) * mm, "end": v(16348.08, -19812) * mm});
            skLineSegment(sketch, "E232", {"start": v(15738.48, -19659.6) * mm, "end": v(15738.48, -19812) * mm, "construction": true});
            skPoint(sketch, "E233", {"position": v(2578.1, -19735.8) * mm});
            skLineSegment(sketch, "E234.bottom", {"start": v(1968.5, -19659.6) * mm, "end": v(3187.7, -19659.6) * mm});
            skLineSegment(sketch, "E234.top", {"start": v(1968.5, -19812) * mm, "end": v(3187.7, -19812) * mm});
            skLineSegment(sketch, "E234.left", {"start": v(1968.5, -19659.6) * mm, "end": v(1968.5, -19812) * mm});
            skLineSegment(sketch, "E234.right", {"start": v(3187.7, -19659.6) * mm, "end": v(3187.7, -19812) * mm});
            skLineSegment(sketch, "E235", {"start": v(2578.1, -19659.6) * mm, "end": v(2578.1, -19812) * mm, "construction": true});
            skLineSegment(sketch, "E236", {"start": v(22532.98, -19659.6) * mm, "end": v(22532.98, -11233.15) * mm});
            skLineSegment(sketch, "E237", {"start": v(28057.48, -19659.6) * mm, "end": v(28057.48, -11233.15) * mm});
            skLineSegment(sketch, "E238", {"start": v(17008.48, -19659.6) * mm, "end": v(17008.48, -11233.15) * mm});
            skLineSegment(sketch, "E239", {"start": v(16894.18, -11233.15) * mm, "end": v(16894.18, -19659.6) * mm});
            skLineSegment(sketch, "E240", {"start": v(22418.68, -11233.15) * mm, "end": v(22418.68, -19659.6) * mm});
            skLineSegment(sketch, "E241", {"start": v(27943.18, -11233.15) * mm, "end": v(27943.18, -19659.6) * mm});
            skLineSegment(sketch, "E242", {"start": v(30858.58, -11233.15) * mm, "end": v(32619.95, -12994.52) * mm});
            skLineSegment(sketch, "E243", {"start": v(32734.25, -13108.82) * mm, "end": v(33822.52, -12020.55) * mm});
            skLineSegment(sketch, "E244", {"start": v(33794.7, -11906.25) * mm, "end": v(32734.25, -10845.8) * mm});
            skLineSegment(sketch, "E245", {"start": v(32619.95, -10893.14) * mm, "end": v(33704.12, -11977.31) * mm});
            skLineSegment(sketch, "E246", {"start": v(33704.12, -11977.31) * mm, "end": v(32734.25, -12947.18) * mm});
            skLineSegment(sketch, "E247", {"start": v(32734.25, -12947.18) * mm, "end": v(30905.92, -11118.85) * mm});
            skLineSegment(sketch, "E248.trimOffspring", {"start": v(33822.52, -12020.55) * mm, "end": v(36423.6, -12020.55) * mm});
            skLineSegment(sketch, "E249.trimOffspring", {"start": v(33794.7, -11906.25) * mm, "end": v(36423.6, -11906.25) * mm});
            skLineSegment(sketch, "E250", {"start": v(32734.25, -13108.82) * mm, "end": v(32734.25, -15728.95) * mm});
            skLineSegment(sketch, "E251", {"start": v(32619.95, -12994.52) * mm, "end": v(32619.95, -15843.25) * mm});
            skLineSegment(sketch, "E252", {"start": v(36423.6, -15728.95) * mm, "end": v(32734.25, -15728.95) * mm});
            skLineSegment(sketch, "E253", {"start": v(36423.6, -15843.25) * mm, "end": v(32619.95, -15843.25) * mm});
            skLineSegment(sketch, "E254", {"start": v(26190.58, -19659.6) * mm, "end": v(26190.58, -17068.8) * mm});
            skLineSegment(sketch, "E255", {"start": v(22418.68, -17068.8) * mm, "end": v(26190.58, -17068.8) * mm});
            skLineSegment(sketch, "E256", {"start": v(22532.98, -16954.5) * mm, "end": v(26304.88, -16954.5) * mm});
            skLineSegment(sketch, "E257", {"start": v(26304.88, -17068.8) * mm, "end": v(26304.88, -19659.6) * mm});
            skLineSegment(sketch, "E258", {"start": v(26304.88, -16954.5) * mm, "end": v(27943.18, -16954.5) * mm});
            skLineSegment(sketch, "E259", {"start": v(26304.88, -17068.8) * mm, "end": v(27943.18, -17068.8) * mm});
            skLineSegment(sketch, "E260", {"start": v(11918.95, -19659.6) * mm, "end": v(11918.95, -11118.85) * mm});
            skLineSegment(sketch, "E261", {"start": v(12033.25, -19659.6) * mm, "end": v(12033.25, -11233.15) * mm});
            skLineSegment(sketch, "E262.trimOffspring", {"start": v(17008.48, -11233.15) * mm, "end": v(30858.58, -11233.15) * mm});
            skLineSegment(sketch, "E263.bottom", {"start": v(6686.55, -3403.6) * mm, "end": v(7651.75, -3403.6) * mm});
            skLineSegment(sketch, "E263.top", {"start": v(6686.55, -3517.9) * mm, "end": v(7651.75, -3517.9) * mm});
            skLineSegment(sketch, "E263.left", {"start": v(6686.55, -3403.6) * mm, "end": v(6686.55, -3517.9) * mm});
            skLineSegment(sketch, "E263.right", {"start": v(7651.75, -3403.6) * mm, "end": v(7651.75, -3517.9) * mm});
            skLineSegment(sketch, "E264.bottom", {"start": v(9448.8, -3403.6) * mm, "end": v(10414, -3403.6) * mm});
            skLineSegment(sketch, "E264.top", {"start": v(9448.8, -3517.9) * mm, "end": v(10414, -3517.9) * mm});
            skLineSegment(sketch, "E264.left", {"start": v(9448.8, -3403.6) * mm, "end": v(9448.8, -3517.9) * mm});
            skLineSegment(sketch, "E264.right", {"start": v(10414, -3403.6) * mm, "end": v(10414, -3517.9) * mm});
            skLineSegment(sketch, "E265.bottom", {"start": v(12211.05, -3403.6) * mm, "end": v(13176.25, -3403.6) * mm});
            skLineSegment(sketch, "E265.top", {"start": v(12211.05, -3517.9) * mm, "end": v(13176.25, -3517.9) * mm});
            skLineSegment(sketch, "E265.left", {"start": v(12211.05, -3403.6) * mm, "end": v(12211.05, -3517.9) * mm});
            skLineSegment(sketch, "E265.right", {"start": v(13176.25, -3403.6) * mm, "end": v(13176.25, -3517.9) * mm});
            skLineSegment(sketch, "E266.bottom", {"start": v(23260.05, -3403.6) * mm, "end": v(24225.25, -3403.6) * mm});
            skLineSegment(sketch, "E266.top", {"start": v(23260.05, -3517.9) * mm, "end": v(24225.25, -3517.9) * mm});
            skLineSegment(sketch, "E266.left", {"start": v(23260.05, -3403.6) * mm, "end": v(23260.05, -3517.9) * mm});
            skLineSegment(sketch, "E266.right", {"start": v(24225.25, -3403.6) * mm, "end": v(24225.25, -3517.9) * mm});
            skLineSegment(sketch, "E267.bottom", {"start": v(17735.55, -3403.6) * mm, "end": v(18700.75, -3403.6) * mm});
            skLineSegment(sketch, "E267.top", {"start": v(17735.55, -3517.9) * mm, "end": v(18700.75, -3517.9) * mm});
            skLineSegment(sketch, "E267.left", {"start": v(17735.55, -3403.6) * mm, "end": v(17735.55, -3517.9) * mm});
            skLineSegment(sketch, "E267.right", {"start": v(18700.75, -3403.6) * mm, "end": v(18700.75, -3517.9) * mm});
            skLineSegment(sketch, "E268.bottom", {"start": v(18967.45, -3403.6) * mm, "end": v(19932.65, -3403.6) * mm});
            skLineSegment(sketch, "E268.top", {"start": v(18967.45, -3517.9) * mm, "end": v(19932.65, -3517.9) * mm});
            skLineSegment(sketch, "E268.left", {"start": v(18967.45, -3403.6) * mm, "end": v(18967.45, -3517.9) * mm});
            skLineSegment(sketch, "E268.right", {"start": v(19932.65, -3403.6) * mm, "end": v(19932.65, -3517.9) * mm});
            skLineSegment(sketch, "E269.bottom", {"start": v(13442.95, -3403.6) * mm, "end": v(14408.15, -3403.6) * mm});
            skLineSegment(sketch, "E269.top", {"start": v(13442.95, -3517.9) * mm, "end": v(14408.15, -3517.9) * mm});
            skLineSegment(sketch, "E269.left", {"start": v(13442.95, -3403.6) * mm, "end": v(13442.95, -3517.9) * mm});
            skLineSegment(sketch, "E269.right", {"start": v(14408.15, -3403.6) * mm, "end": v(14408.15, -3517.9) * mm});
            skLineSegment(sketch, "E270.bottom", {"start": v(35382.2, -3403.6) * mm, "end": v(36347.4, -3403.6) * mm});
            skLineSegment(sketch, "E270.top", {"start": v(35382.2, -3517.9) * mm, "end": v(36347.4, -3517.9) * mm});
            skLineSegment(sketch, "E270.left", {"start": v(35382.2, -3403.6) * mm, "end": v(35382.2, -3517.9) * mm});
            skLineSegment(sketch, "E270.right", {"start": v(36347.4, -3403.6) * mm, "end": v(36347.4, -3517.9) * mm});
            skLineSegment(sketch, "E271.bottom", {"start": v(31264.22, -3403.6) * mm, "end": v(32229.42, -3403.6) * mm});
            skLineSegment(sketch, "E271.top", {"start": v(31264.22, -3517.9) * mm, "end": v(32229.42, -3517.9) * mm});
            skLineSegment(sketch, "E271.left", {"start": v(31264.22, -3403.6) * mm, "end": v(31264.22, -3517.9) * mm});
            skLineSegment(sketch, "E271.right", {"start": v(32229.42, -3403.6) * mm, "end": v(32229.42, -3517.9) * mm});
            skLineSegment(sketch, "E272.bottom", {"start": v(28711.52, -3403.6) * mm, "end": v(29676.72, -3403.6) * mm});
            skLineSegment(sketch, "E272.top", {"start": v(28711.52, -3517.9) * mm, "end": v(29676.72, -3517.9) * mm});
            skLineSegment(sketch, "E272.left", {"start": v(28711.52, -3403.6) * mm, "end": v(28711.52, -3517.9) * mm});
            skLineSegment(sketch, "E272.right", {"start": v(29676.72, -3403.6) * mm, "end": v(29676.72, -3517.9) * mm});
            skLineSegment(sketch, "E273.bottom", {"start": v(24491.95, -3403.6) * mm, "end": v(25457.15, -3403.6) * mm});
            skLineSegment(sketch, "E273.top", {"start": v(24491.95, -3517.9) * mm, "end": v(25457.15, -3517.9) * mm});
            skLineSegment(sketch, "E273.left", {"start": v(24491.95, -3403.6) * mm, "end": v(24491.95, -3517.9) * mm});
            skLineSegment(sketch, "E273.right", {"start": v(25457.15, -3403.6) * mm, "end": v(25457.15, -3517.9) * mm});
            skLineSegment(sketch, "E274.bottom", {"start": v(32619.95, -7042.15) * mm, "end": v(32734.25, -7042.15) * mm});
            skLineSegment(sketch, "E274.top", {"start": v(32619.95, -8007.35) * mm, "end": v(32734.25, -8007.35) * mm});
            skLineSegment(sketch, "E274.left", {"start": v(32619.95, -7042.15) * mm, "end": v(32619.95, -8007.35) * mm});
            skLineSegment(sketch, "E274.right", {"start": v(32734.25, -7042.15) * mm, "end": v(32734.25, -8007.35) * mm});
            skLineSegment(sketch, "E275.bottom", {"start": v(30092.65, -9632.95) * mm, "end": v(31057.85, -9632.95) * mm});
            skLineSegment(sketch, "E275.top", {"start": v(30092.65, -9747.25) * mm, "end": v(31057.85, -9747.25) * mm});
            skLineSegment(sketch, "E275.left", {"start": v(30092.65, -9632.95) * mm, "end": v(30092.65, -9747.25) * mm});
            skLineSegment(sketch, "E275.right", {"start": v(31057.85, -9632.95) * mm, "end": v(31057.85, -9747.25) * mm});
            skLineSegment(sketch, "E276.bottom", {"start": v(26723.98, -9632.95) * mm, "end": v(27689.18, -9632.95) * mm});
            skLineSegment(sketch, "E276.top", {"start": v(26723.98, -9747.25) * mm, "end": v(27689.18, -9747.25) * mm});
            skLineSegment(sketch, "E276.left", {"start": v(26723.98, -9632.95) * mm, "end": v(26723.98, -9747.25) * mm});
            skLineSegment(sketch, "E276.right", {"start": v(27689.18, -9632.95) * mm, "end": v(27689.18, -9747.25) * mm});
            skLineSegment(sketch, "E277.bottom", {"start": v(23355.3, -9632.95) * mm, "end": v(24320.5, -9632.95) * mm});
            skLineSegment(sketch, "E277.top", {"start": v(23355.3, -9747.25) * mm, "end": v(24320.5, -9747.25) * mm});
            skLineSegment(sketch, "E277.left", {"start": v(23355.3, -9632.95) * mm, "end": v(23355.3, -9747.25) * mm});
            skLineSegment(sketch, "E277.right", {"start": v(24320.5, -9632.95) * mm, "end": v(24320.5, -9747.25) * mm});
            skLineSegment(sketch, "E278.bottom", {"start": v(4813.3, -7254.88) * mm, "end": v(4927.6, -7254.88) * mm});
            skLineSegment(sketch, "E278.top", {"start": v(4813.3, -8220.08) * mm, "end": v(4927.6, -8220.08) * mm});
            skLineSegment(sketch, "E278.left", {"start": v(4813.3, -7254.88) * mm, "end": v(4813.3, -8220.08) * mm});
            skLineSegment(sketch, "E278.right", {"start": v(4927.6, -7254.88) * mm, "end": v(4927.6, -8220.08) * mm});
            skLineSegment(sketch, "E279.bottom", {"start": v(23355.3, -4889.5) * mm, "end": v(24320.5, -4889.5) * mm});
            skLineSegment(sketch, "E279.top", {"start": v(23355.3, -5003.8) * mm, "end": v(24320.5, -5003.8) * mm});
            skLineSegment(sketch, "E279.left", {"start": v(23355.3, -4889.5) * mm, "end": v(23355.3, -5003.8) * mm});
            skLineSegment(sketch, "E279.right", {"start": v(24320.5, -4889.5) * mm, "end": v(24320.5, -5003.8) * mm});
            skLineSegment(sketch, "E280.bottom", {"start": v(26723.98, -4889.5) * mm, "end": v(27689.18, -4889.5) * mm});
            skLineSegment(sketch, "E280.top", {"start": v(26723.98, -5003.8) * mm, "end": v(27689.18, -5003.8) * mm});
            skLineSegment(sketch, "E280.left", {"start": v(26723.98, -4889.5) * mm, "end": v(26723.98, -5003.8) * mm});
            skLineSegment(sketch, "E280.right", {"start": v(27689.18, -4889.5) * mm, "end": v(27689.18, -5003.8) * mm});
            skLineSegment(sketch, "E281.bottom", {"start": v(30092.65, -4889.5) * mm, "end": v(31057.85, -4889.5) * mm});
            skLineSegment(sketch, "E281.top", {"start": v(30092.65, -5003.8) * mm, "end": v(31057.85, -5003.8) * mm});
            skLineSegment(sketch, "E281.left", {"start": v(30092.65, -4889.5) * mm, "end": v(30092.65, -5003.8) * mm});
            skLineSegment(sketch, "E281.right", {"start": v(31057.85, -4889.5) * mm, "end": v(31057.85, -5003.8) * mm});
            skLineSegment(sketch, "E282.bottom", {"start": v(4076.92, -3717.9) * mm, "end": v(4157.74, -3637.09) * mm});
            skLineSegment(sketch, "E282.top", {"start": v(4759.42, -4400.4) * mm, "end": v(4840.24, -4319.59) * mm});
            skLineSegment(sketch, "E282.left", {"start": v(4076.92, -3717.9) * mm, "end": v(4759.42, -4400.4) * mm});
            skLineSegment(sketch, "E282.right", {"start": v(4157.74, -3637.09) * mm, "end": v(4840.24, -4319.59) * mm});
            skLineSegment(sketch, "E283.bottom", {"start": v(33470.63, -12210.8) * mm, "end": v(33551.45, -12291.62) * mm});
            skLineSegment(sketch, "E283.top", {"start": v(32788.13, -12893.3) * mm, "end": v(32868.95, -12974.12) * mm});
            skLineSegment(sketch, "E283.left", {"start": v(33470.63, -12210.8) * mm, "end": v(32788.13, -12893.3) * mm});
            skLineSegment(sketch, "E283.right", {"start": v(33551.45, -12291.62) * mm, "end": v(32868.95, -12974.12) * mm});
            skLineSegment(sketch, "E284.bottom", {"start": v(32707.3, -10980.5) * mm, "end": v(32788.13, -10899.68) * mm});
            skLineSegment(sketch, "E284.top", {"start": v(33389.8, -11663) * mm, "end": v(33470.63, -11582.18) * mm});
            skLineSegment(sketch, "E284.left", {"start": v(32707.3, -10980.5) * mm, "end": v(33389.8, -11663) * mm});
            skLineSegment(sketch, "E284.right", {"start": v(32788.13, -10899.68) * mm, "end": v(33470.63, -11582.18) * mm});
            skLineSegment(sketch, "E285.bottom", {"start": v(4678.6, -2487.61) * mm, "end": v(4759.42, -2568.44) * mm});
            skLineSegment(sketch, "E285.top", {"start": v(3996.1, -3170.11) * mm, "end": v(4076.92, -3250.94) * mm});
            skLineSegment(sketch, "E285.left", {"start": v(4678.6, -2487.61) * mm, "end": v(3996.1, -3170.11) * mm});
            skLineSegment(sketch, "E285.right", {"start": v(4759.42, -2568.44) * mm, "end": v(4076.92, -3250.94) * mm});
            skSolve(sketch);
        }
        {
            var Q0;
            {var subQ4=sQuery(id+"F0.wireOp",EDGE,"E67.left");Q0=makeQuery(id+"F0.imprint","IMPRINT",FACE,{"disambiguationData":[TD([[makeQuery(id+"F0.imprint","IMPRINT",EDGE,{"derivedFrom":subQ4}),-1.0]])]});}
            var Q1;
            {var subQ2=sQuery(id+"F0.wireOp",EDGE,"E90.left");Q1=makeQuery(id+"F0.imprint","IMPRINT",FACE,{"disambiguationData":[TD([[makeQuery(id+"F0.imprint","IMPRINT",EDGE,{"derivedFrom":subQ2}),1.0]])]});}
            var Q2;
            {var subQ4=sQuery(id+"F0.wireOp",EDGE,"E82.left");Q2=makeQuery(id+"F0.imprint","IMPRINT",FACE,{"disambiguationData":[TD([[makeQuery(id+"F0.imprint","IMPRINT",EDGE,{"derivedFrom":subQ4}),-1.0]])]});}
            var Q3;
            {var subQ0=sQuery(id+"F0.wireOp",EDGE,"E82.left");Q3=makeQuery(id+"F0.imprint","IMPRINT",FACE,{"disambiguationData":[TD([[makeQuery(id+"F0.imprint","IMPRINT",EDGE,{"derivedFrom":subQ0}),1.0]])]});}
            var Q4;
            {var subQ2=sQuery(id+"F0.wireOp",EDGE,"E84.left");Q4=makeQuery(id+"F0.imprint","IMPRINT",FACE,{"disambiguationData":[TD([[makeQuery(id+"F0.imprint","IMPRINT",EDGE,{"derivedFrom":subQ2}),1.0]])]});}
            var Q5;
            {var subQ3=sQuery(id+"F0.wireOp",EDGE,"E84.left");Q5=makeQuery(id+"F0.imprint","IMPRINT",FACE,{"disambiguationData":[TD([[makeQuery(id+"F0.imprint","IMPRINT",EDGE,{"derivedFrom":subQ3}),-1.0]])]});}
            var Q6;
            {var subQ0=sQuery(id+"F0.wireOp",EDGE,"E56.left");Q6=makeQuery(id+"F0.imprint","IMPRINT",FACE,{"disambiguationData":[TD([[makeQuery(id+"F0.imprint","IMPRINT",EDGE,{"derivedFrom":subQ0}),1.0]])]});}
            var Q7;
            {var subQ0=sQuery(id+"F0.wireOp",EDGE,"E86.left");Q7=makeQuery(id+"F0.imprint","IMPRINT",FACE,{"disambiguationData":[TD([[makeQuery(id+"F0.imprint","IMPRINT",EDGE,{"derivedFrom":subQ0}),1.0]])]});}
            var Q8;
            {var subQ1=sQuery(id+"F0.wireOp",EDGE,"E11");Q8=makeQuery(id+"F0.imprint","IMPRINT",FACE,{"disambiguationData":[TD([[makeQuery(id+"F0.imprint","IMPRINT",EDGE,{"derivedFrom":subQ1}),-1.0]])]});}
            var Q9;
            {var subQ2=sQuery(id+"F0.wireOp",EDGE,"E60.left");Q9=makeQuery(id+"F0.imprint","IMPRINT",FACE,{"disambiguationData":[TD([[makeQuery(id+"F0.imprint","IMPRINT",EDGE,{"derivedFrom":subQ2}),1.0]])]});}
            var Q10;
            {var subQ0=sQuery(id+"F0.wireOp",EDGE,"E77.left");Q10=makeQuery(id+"F0.imprint","IMPRINT",FACE,{"disambiguationData":[TD([[makeQuery(id+"F0.imprint","IMPRINT",EDGE,{"derivedFrom":subQ0}),1.0]])]});}
            var Q11;
            {var subQ2=sQuery(id+"F0.wireOp",EDGE,"E75.right");Q11=makeQuery(id+"F0.imprint","IMPRINT",FACE,{"disambiguationData":[TD([[makeQuery(id+"F0.imprint","IMPRINT",EDGE,{"derivedFrom":subQ2}),1.0]])]});}
            var Q12;
            {var subQ0=sQuery(id+"F0.wireOp",EDGE,"E75.left");Q12=makeQuery(id+"F0.imprint","IMPRINT",FACE,{"disambiguationData":[TD([[makeQuery(id+"F0.imprint","IMPRINT",EDGE,{"derivedFrom":subQ0}),1.0]])]});}
            var Q13;
            {var subQ11=sQuery(id+"F0.wireOp",EDGE,"E7");Q13=makeQuery(id+"F0.imprint","IMPRINT",FACE,{"disambiguationData":[TD([[makeQuery(id+"F0.imprint","IMPRINT",EDGE,{"derivedFrom":subQ11}),-1.0]])]});}
            var Q14;
            {var subQ2=sQuery(id+"F0.wireOp",EDGE,"E50.left");Q14=makeQuery(id+"F0.imprint","IMPRINT",FACE,{"disambiguationData":[TD([[makeQuery(id+"F0.imprint","IMPRINT",EDGE,{"derivedFrom":subQ2}),1.0]])]});}
            var Q15;
            {var subQ2=sQuery(id+"F0.wireOp",EDGE,"E57.left");Q15=makeQuery(id+"F0.imprint","IMPRINT",FACE,{"disambiguationData":[TD([[makeQuery(id+"F0.imprint","IMPRINT",EDGE,{"derivedFrom":subQ2}),1.0]])]});}
            var Q16;
            {var subQ2=sQuery(id+"F0.wireOp",EDGE,"E51.left");Q16=makeQuery(id+"F0.imprint","IMPRINT",FACE,{"disambiguationData":[TD([[makeQuery(id+"F0.imprint","IMPRINT",EDGE,{"derivedFrom":subQ2}),1.0]])]});}
            var Q17;
            {var subQ0=sQuery(id+"F0.wireOp",EDGE,"E73.left");Q17=makeQuery(id+"F0.imprint","IMPRINT",FACE,{"disambiguationData":[TD([[makeQuery(id+"F0.imprint","IMPRINT",EDGE,{"derivedFrom":subQ0}),1.0]])]});}
            var Q18;
            {var subQ0=sQuery(id+"F0.wireOp",EDGE,"E69.left");Q18=makeQuery(id+"F0.imprint","IMPRINT",FACE,{"disambiguationData":[TD([[makeQuery(id+"F0.imprint","IMPRINT",EDGE,{"derivedFrom":subQ0}),1.0]])]});}
            var Q19;
            {var subQ3=sQuery(id+"F0.wireOp",EDGE,"E61.right");Q19=makeQuery(id+"F0.imprint","IMPRINT",FACE,{"disambiguationData":[TD([[makeQuery(id+"F0.imprint","IMPRINT",EDGE,{"derivedFrom":subQ3}),1.0]])]});}
            var Q20;
            {var subQ2=sQuery(id+"F0.wireOp",EDGE,"E53.left");Q20=makeQuery(id+"F0.imprint","IMPRINT",FACE,{"disambiguationData":[TD([[makeQuery(id+"F0.imprint","IMPRINT",EDGE,{"derivedFrom":subQ2}),1.0]])]});}
            var Q21;
            {var subQ0=sQuery(id+"F0.wireOp",EDGE,"E61.left");Q21=makeQuery(id+"F0.imprint","IMPRINT",FACE,{"disambiguationData":[TD([[makeQuery(id+"F0.imprint","IMPRINT",EDGE,{"derivedFrom":subQ0}),1.0]])]});}
            var Q22;
            {var subQ4=sQuery(id+"F0.wireOp",EDGE,"E1");Q22=makeQuery(id+"F0.imprint","IMPRINT",FACE,{"disambiguationData":[TD([[makeQuery(id+"F0.imprint","IMPRINT",EDGE,{"derivedFrom":subQ4}),-1.0]])]});}
            var Q23;
            {var subQ0=sQuery(id+"F0.wireOp",EDGE,"E65.left");Q23=makeQuery(id+"F0.imprint","IMPRINT",FACE,{"disambiguationData":[TD([[makeQuery(id+"F0.imprint","IMPRINT",EDGE,{"derivedFrom":subQ0}),1.0]])]});}
            var Q24;
            {var subQ3=sQuery(id+"F0.wireOp",EDGE,"E63.right");Q24=makeQuery(id+"F0.imprint","IMPRINT",FACE,{"disambiguationData":[TD([[makeQuery(id+"F0.imprint","IMPRINT",EDGE,{"derivedFrom":subQ3}),1.0]])]});}
            var Q25;
            {var subQ0=sQuery(id+"F0.wireOp",EDGE,"E63.left");Q25=makeQuery(id+"F0.imprint","IMPRINT",FACE,{"disambiguationData":[TD([[makeQuery(id+"F0.imprint","IMPRINT",EDGE,{"derivedFrom":subQ0}),1.0]])]});}
            var Q26;
            {var subQ4=sQuery(id+"F0.wireOp",EDGE,"E63.left");Q26=makeQuery(id+"F0.imprint","IMPRINT",FACE,{"disambiguationData":[TD([[makeQuery(id+"F0.imprint","IMPRINT",EDGE,{"derivedFrom":subQ4}),-1.0]])]});}
            var Q27;
            {var subQ2=sQuery(id+"F0.wireOp",EDGE,"E67.left");Q27=makeQuery(id+"F0.imprint","IMPRINT",FACE,{"disambiguationData":[TD([[makeQuery(id+"F0.imprint","IMPRINT",EDGE,{"derivedFrom":subQ2}),1.0]])]});}
            var Q28;
            {var subQ2=sQuery(id+"F0.wireOp",EDGE,"E52.left");Q28=makeQuery(id+"F0.imprint","IMPRINT",FACE,{"disambiguationData":[TD([[makeQuery(id+"F0.imprint","IMPRINT",EDGE,{"derivedFrom":subQ2}),1.0]])]});}
            var Q29;
            {var subQ0=sQuery(id+"F0.wireOp",EDGE,"E71.left");Q29=makeQuery(id+"F0.imprint","IMPRINT",FACE,{"disambiguationData":[TD([[makeQuery(id+"F0.imprint","IMPRINT",EDGE,{"derivedFrom":subQ0}),1.0]])]});}
            var Q30;
            {var subQ3=sQuery(id+"F0.wireOp",EDGE,"E71.right");Q30=makeQuery(id+"F0.imprint","IMPRINT",FACE,{"disambiguationData":[TD([[makeQuery(id+"F0.imprint","IMPRINT",EDGE,{"derivedFrom":subQ3}),1.0]])]});}
            var Q31;
            {var subQ3=sQuery(id+"F0.wireOp",EDGE,"E3");Q31=makeQuery(id+"F0.imprint","IMPRINT",FACE,{"disambiguationData":[TD([[makeQuery(id+"F0.imprint","IMPRINT",EDGE,{"derivedFrom":subQ3}),-1.0]])]});}
            var Q32;
            {var subQ0=sQuery(id+"F0.wireOp",EDGE,"E55.left");Q32=makeQuery(id+"F0.imprint","IMPRINT",FACE,{"disambiguationData":[TD([[makeQuery(id+"F0.imprint","IMPRINT",EDGE,{"derivedFrom":subQ0}),1.0]])]});}
            var Q33;
            {var subQ2=sQuery(id+"F0.wireOp",EDGE,"E54.left");Q33=makeQuery(id+"F0.imprint","IMPRINT",FACE,{"disambiguationData":[TD([[makeQuery(id+"F0.imprint","IMPRINT",EDGE,{"derivedFrom":subQ2}),1.0]])]});}
            var Q34;
            {var subQ5=sQuery(id+"F0.wireOp",EDGE,"E17.bottom");Q34=makeQuery(id+"F0.imprint","IMPRINT",FACE,{"disambiguationData":[TD([[makeQuery(id+"F0.imprint","IMPRINT",EDGE,{"derivedFrom":subQ5}),-1.0]])]});}
            var Q35;
            {var subQ0=sQuery(id+"F0.wireOp",EDGE,"E111.left");Q35=makeQuery(id+"F0.imprint","IMPRINT",FACE,{"disambiguationData":[TD([[makeQuery(id+"F0.imprint","IMPRINT",EDGE,{"derivedFrom":subQ0}),1.0]])]});}
            var Q36;
            {var subQ3=sQuery(id+"F0.wireOp",EDGE,"E79.right");Q36=makeQuery(id+"F0.imprint","IMPRINT",FACE,{"disambiguationData":[TD([[makeQuery(id+"F0.imprint","IMPRINT",EDGE,{"derivedFrom":subQ3}),1.0]])]});}
            var Q37;
            Q37=makeQuery(id+"F0.imprint","IMPRINT",FACE,{"disambiguationData":[TD([[makeQuery(id+"F0.imprint","IMPRINT",EDGE,{"derivedFrom":sQuery(id+"F0.wireOp",EDGE,"E79.bottom")}),-1.0]])]});
            var Q38;
            {var subQ2=sQuery(id+"F0.wireOp",EDGE,"E79.left");Q38=makeQuery(id+"F0.imprint","IMPRINT",FACE,{"disambiguationData":[TD([[makeQuery(id+"F0.imprint","IMPRINT",EDGE,{"derivedFrom":subQ2}),-1.0]])]});}
            var Q39;
            Q39=makeQuery(id+"F0.imprint","IMPRINT",FACE,{"disambiguationData":[TD([[makeQuery(id+"F0.imprint","IMPRINT",EDGE,{"derivedFrom":sQuery(id+"F0.wireOp",EDGE,"E118.bottom")}),-1.0]])]});
            var Q40;
            {var subQ5=sQuery(id+"F0.wireOp",EDGE,"E107.right");Q40=makeQuery(id+"F0.imprint","IMPRINT",FACE,{"disambiguationData":[TD([[makeQuery(id+"F0.imprint","IMPRINT",EDGE,{"derivedFrom":subQ5}),1.0]])]});}
            var Q41;
            Q41=makeQuery(id+"F0.imprint","IMPRINT",FACE,{"disambiguationData":[TD([[makeQuery(id+"F0.imprint","IMPRINT",EDGE,{"derivedFrom":sQuery(id+"F0.wireOp",EDGE,"E107.bottom")}),-1.0]])]});
            var Q42;
            {var subQ2=sQuery(id+"F0.wireOp",EDGE,"E133");Q42=makeQuery(id+"F0.imprint","IMPRINT",FACE,{"disambiguationData":[TD([[makeQuery(id+"F0.imprint","IMPRINT",EDGE,{"derivedFrom":subQ2}),1.0]])]});}
            var Q43;
            {var subQ0=sQuery(id+"F0.wireOp",EDGE,"E122");Q43=makeQuery(id+"F0.imprint","IMPRINT",FACE,{"disambiguationData":[TD([[makeQuery(id+"F0.imprint","IMPRINT",EDGE,{"derivedFrom":subQ0}),1.0]])]});}
            var Q44;
            {var subQ1=sQuery(id+"F0.wireOp",EDGE,"E114.left");Q44=makeQuery(id+"F0.imprint","IMPRINT",FACE,{"disambiguationData":[TD([[makeQuery(id+"F0.imprint","IMPRINT",EDGE,{"derivedFrom":subQ1}),-1.0]])]});}
            var Q45;
            Q45=makeQuery(id+"F0.imprint","IMPRINT",FACE,{"disambiguationData":[TD([[makeQuery(id+"F0.imprint","IMPRINT",EDGE,{"derivedFrom":sQuery(id+"F0.wireOp",EDGE,"E114.bottom")}),-1.0]])]});
            var Q46;
            {var subQ0=sQuery(id+"F0.wireOp",EDGE,"E103.left");Q46=makeQuery(id+"F0.imprint","IMPRINT",FACE,{"disambiguationData":[TD([[makeQuery(id+"F0.imprint","IMPRINT",EDGE,{"derivedFrom":subQ0}),-1.0]])]});}
            var Q47;
            Q47=makeQuery(id+"F0.imprint","IMPRINT",FACE,{"disambiguationData":[TD([[makeQuery(id+"F0.imprint","IMPRINT",EDGE,{"derivedFrom":sQuery(id+"F0.wireOp",EDGE,"E103.bottom")}),-1.0]])]});
            var Q48;
            {var subQ0=sQuery(id+"F0.wireOp",EDGE,"E103.right");Q48=makeQuery(id+"F0.imprint","IMPRINT",FACE,{"disambiguationData":[TD([[makeQuery(id+"F0.imprint","IMPRINT",EDGE,{"derivedFrom":subQ0}),1.0]])]});}
            var Q49;
            {var subQ2=sQuery(id+"F0.wireOp",EDGE,"E136.bottom");Q49=makeQuery(id+"F0.imprint","IMPRINT",FACE,{"disambiguationData":[TD([[makeQuery(id+"F0.imprint","IMPRINT",EDGE,{"derivedFrom":subQ2}),1.0]])]});}
            var Q50;
            {var subQ0=sQuery(id+"F0.wireOp",EDGE,"E136.top");Q50=makeQuery(id+"F0.imprint","IMPRINT",FACE,{"disambiguationData":[TD([[makeQuery(id+"F0.imprint","IMPRINT",EDGE,{"derivedFrom":subQ0}),-1.0]])]});}
            var Q51;
            {var subQ2=sQuery(id+"F0.wireOp",EDGE,"E279.right");var subQ9=sQuery(id+"F0.wireOp",EDGE,"E280.right");Q51=qUnion([makeQuery(id+"F0.imprint","IMPRINT",FACE,{"disambiguationData":[TD([[makeQuery(id+"F0.imprint","IMPRINT",EDGE,{"derivedFrom":subQ9}),1.0]])]}),makeQuery(id+"F0.imprint","IMPRINT",FACE,{"disambiguationData":[TD([[makeQuery(id+"F0.imprint","IMPRINT",EDGE,{"derivedFrom":subQ2}),1.0]])]})]);}
            var Q52;
            {var subQ5=sQuery(id+"F0.wireOp",EDGE,"E140");Q52=makeQuery(id+"F0.imprint","IMPRINT",FACE,{"disambiguationData":[TD([[makeQuery(id+"F0.imprint","IMPRINT",EDGE,{"derivedFrom":subQ5}),-1.0]])]});}
            var Q53;
            {var subQ0=sQuery(id+"F0.wireOp",EDGE,"E82.right");Q53=makeQuery(id+"F0.imprint","IMPRINT",FACE,{"disambiguationData":[TD([[makeQuery(id+"F0.imprint","IMPRINT",EDGE,{"derivedFrom":subQ0}),1.0]])]});}
            var Q54;
            {var subQ0=sQuery(id+"F0.wireOp",EDGE,"E154.left");Q54=makeQuery(id+"F0.imprint","IMPRINT",FACE,{"disambiguationData":[TD([[makeQuery(id+"F0.imprint","IMPRINT",EDGE,{"derivedFrom":subQ0}),1.0]])]});}
            var Q55;
            {var subQ4=sQuery(id+"F0.wireOp",EDGE,"E154.left");Q55=makeQuery(id+"F0.imprint","IMPRINT",FACE,{"disambiguationData":[TD([[makeQuery(id+"F0.imprint","IMPRINT",EDGE,{"derivedFrom":subQ4}),-1.0]])]});}
            var Q56;
            {var subQ0=sQuery(id+"F0.wireOp",EDGE,"E158.left");Q56=makeQuery(id+"F0.imprint","IMPRINT",FACE,{"disambiguationData":[TD([[makeQuery(id+"F0.imprint","IMPRINT",EDGE,{"derivedFrom":subQ0}),1.0]])]});}
            var Q57;
            {var subQ2=sQuery(id+"F0.wireOp",EDGE,"E158.left");Q57=makeQuery(id+"F0.imprint","IMPRINT",FACE,{"disambiguationData":[TD([[makeQuery(id+"F0.imprint","IMPRINT",EDGE,{"derivedFrom":subQ2}),-1.0]])]});}
            var Q58;
            {var subQ2=sQuery(id+"F0.wireOp",EDGE,"E162.left");Q58=makeQuery(id+"F0.imprint","IMPRINT",FACE,{"disambiguationData":[TD([[makeQuery(id+"F0.imprint","IMPRINT",EDGE,{"derivedFrom":subQ2}),1.0]])]});}
            var Q59;
            {var subQ4=sQuery(id+"F0.wireOp",EDGE,"E162.left");Q59=makeQuery(id+"F0.imprint","IMPRINT",FACE,{"disambiguationData":[TD([[makeQuery(id+"F0.imprint","IMPRINT",EDGE,{"derivedFrom":subQ4}),-1.0]])]});}
            var Q60;
            {var subQ0=sQuery(id+"F0.wireOp",EDGE,"E166.left");Q60=makeQuery(id+"F0.imprint","IMPRINT",FACE,{"disambiguationData":[TD([[makeQuery(id+"F0.imprint","IMPRINT",EDGE,{"derivedFrom":subQ0}),1.0]])]});}
            var Q61;
            {var subQ2=sQuery(id+"F0.wireOp",EDGE,"E234.left");Q61=makeQuery(id+"F0.imprint","IMPRINT",FACE,{"disambiguationData":[TD([[makeQuery(id+"F0.imprint","IMPRINT",EDGE,{"derivedFrom":subQ2}),1.0]])]});}
            var Q62;
            {var subQ0=sQuery(id+"F0.wireOp",EDGE,"E231.left");Q62=makeQuery(id+"F0.imprint","IMPRINT",FACE,{"disambiguationData":[TD([[makeQuery(id+"F0.imprint","IMPRINT",EDGE,{"derivedFrom":subQ0}),1.0]])]});}
            var Q63;
            {var subQ0=sQuery(id+"F0.wireOp",EDGE,"E190");Q63=makeQuery(id+"F0.imprint","IMPRINT",FACE,{"disambiguationData":[TD([[makeQuery(id+"F0.imprint","IMPRINT",EDGE,{"derivedFrom":subQ0}),-1.0]])]});}
            var Q64;
            {var subQ0=sQuery(id+"F0.wireOp",EDGE,"E213.left");Q64=makeQuery(id+"F0.imprint","IMPRINT",FACE,{"disambiguationData":[TD([[makeQuery(id+"F0.imprint","IMPRINT",EDGE,{"derivedFrom":subQ0}),1.0]])]});}
            var Q65;
            {var subQ0=sQuery(id+"F0.wireOp",EDGE,"E213.right");Q65=makeQuery(id+"F0.imprint","IMPRINT",FACE,{"disambiguationData":[TD([[makeQuery(id+"F0.imprint","IMPRINT",EDGE,{"derivedFrom":subQ0}),1.0]])]});}
            var Q66;
            {var subQ2=sQuery(id+"F0.wireOp",EDGE,"E215.left");Q66=makeQuery(id+"F0.imprint","IMPRINT",FACE,{"disambiguationData":[TD([[makeQuery(id+"F0.imprint","IMPRINT",EDGE,{"derivedFrom":subQ2}),1.0]])]});}
            var Q67;
            {var subQ3=sQuery(id+"F0.wireOp",EDGE,"E184");Q67=makeQuery(id+"F0.imprint","IMPRINT",FACE,{"disambiguationData":[TD([[makeQuery(id+"F0.imprint","IMPRINT",EDGE,{"derivedFrom":subQ3}),-1.0]])]});}
            var Q68;
            {var subQ2=sQuery(id+"F0.wireOp",EDGE,"E202.left");Q68=makeQuery(id+"F0.imprint","IMPRINT",FACE,{"disambiguationData":[TD([[makeQuery(id+"F0.imprint","IMPRINT",EDGE,{"derivedFrom":subQ2}),1.0]])]});}
            var Q69;
            {var subQ0=sQuery(id+"F0.wireOp",EDGE,"E202.right");Q69=makeQuery(id+"F0.imprint","IMPRINT",FACE,{"disambiguationData":[TD([[makeQuery(id+"F0.imprint","IMPRINT",EDGE,{"derivedFrom":subQ0}),1.0]])]});}
            var Q70;
            {var subQ2=sQuery(id+"F0.wireOp",EDGE,"E204.left");Q70=makeQuery(id+"F0.imprint","IMPRINT",FACE,{"disambiguationData":[TD([[makeQuery(id+"F0.imprint","IMPRINT",EDGE,{"derivedFrom":subQ2}),1.0]])]});}
            var Q71;
            {var subQ7=sQuery(id+"F0.wireOp",EDGE,"E178");Q71=makeQuery(id+"F0.imprint","IMPRINT",FACE,{"disambiguationData":[TD([[makeQuery(id+"F0.imprint","IMPRINT",EDGE,{"derivedFrom":subQ7}),-1.0]])]});}
            var Q72;
            {var subQ2=sQuery(id+"F0.wireOp",EDGE,"E221.left");Q72=makeQuery(id+"F0.imprint","IMPRINT",FACE,{"disambiguationData":[TD([[makeQuery(id+"F0.imprint","IMPRINT",EDGE,{"derivedFrom":subQ2}),1.0]])]});}
            var Q73;
            {var subQ0=sQuery(id+"F0.wireOp",EDGE,"E221.right");Q73=makeQuery(id+"F0.imprint","IMPRINT",FACE,{"disambiguationData":[TD([[makeQuery(id+"F0.imprint","IMPRINT",EDGE,{"derivedFrom":subQ0}),1.0]])]});}
            var Q74;
            {var subQ2=sQuery(id+"F0.wireOp",EDGE,"E223.left");Q74=makeQuery(id+"F0.imprint","IMPRINT",FACE,{"disambiguationData":[TD([[makeQuery(id+"F0.imprint","IMPRINT",EDGE,{"derivedFrom":subQ2}),1.0]])]});}
            var Q75;
            {var subQ3=sQuery(id+"F0.wireOp",EDGE,"E176");Q75=makeQuery(id+"F0.imprint","IMPRINT",FACE,{"disambiguationData":[TD([[makeQuery(id+"F0.imprint","IMPRINT",EDGE,{"derivedFrom":subQ3}),-1.0]])]});}
            var Q76;
            {var subQ0=sQuery(id+"F0.wireOp",EDGE,"E228.left");Q76=makeQuery(id+"F0.imprint","IMPRINT",FACE,{"disambiguationData":[TD([[makeQuery(id+"F0.imprint","IMPRINT",EDGE,{"derivedFrom":subQ0}),1.0]])]});}
            var Q77;
            {var subQ4=sQuery(id+"F0.wireOp",EDGE,"E166.left");Q77=makeQuery(id+"F0.imprint","IMPRINT",FACE,{"disambiguationData":[TD([[makeQuery(id+"F0.imprint","IMPRINT",EDGE,{"derivedFrom":subQ4}),-1.0]])]});}
            var Q78;
            {var subQ1=sQuery(id+"F0.wireOp",EDGE,"E236");var subQ5=makeQuery(id+"F0.imprint","INTERSECT",VERTEX,{"derivedFrom":[subQ1,sQuery(id+"F0.wireOp",EDGE,"E256")]});Q78=makeQuery(id+"F0.imprint","IMPRINT",FACE,{"disambiguationData":[TD([[makeQuery(id+"F0.imprint","IMPRINT",EDGE,{"disambiguationData":[TD([[subQ5,-1.0]])],"derivedFrom":subQ1}),1.0]])]});}
            var Q79;
            {var subQ4=sQuery(id+"F0.wireOp",EDGE,"E237");Q79=makeQuery(id+"F0.imprint","IMPRINT",FACE,{"disambiguationData":[TD([[makeQuery(id+"F0.imprint","IMPRINT",EDGE,{"derivedFrom":subQ4}),1.0]])]});}
            var Q80;
            {var subQ1=sQuery(id+"F0.wireOp",EDGE,"E195");var subQ3=sQuery(id+"F0.wireOp",EDGE,"E240");var subQ4=makeQuery(id+"F0.imprint","INTERSECT",VERTEX,{"derivedFrom":[subQ1,subQ3]});Q80=makeQuery(id+"F0.imprint","IMPRINT",FACE,{"disambiguationData":[TD([[makeQuery(id+"F0.imprint","IMPRINT",EDGE,{"disambiguationData":[TD([[subQ4,1.0]])],"derivedFrom":subQ3}),1.0]])]});}
            var Q81;
            {var subQ0=sQuery(id+"F0.wireOp",EDGE,"E254");Q81=makeQuery(id+"F0.imprint","IMPRINT",FACE,{"disambiguationData":[TD([[makeQuery(id+"F0.imprint","IMPRINT",EDGE,{"derivedFrom":subQ0}),-1.0]])]});}
            var Q82;
            {var subQ4=sQuery(id+"F0.wireOp",EDGE,"E231.left");Q82=makeQuery(id+"F0.imprint","IMPRINT",FACE,{"disambiguationData":[TD([[makeQuery(id+"F0.imprint","IMPRINT",EDGE,{"derivedFrom":subQ4}),-1.0]])]});}
            var Q83;
            {var subQ0=sQuery(id+"F0.wireOp",EDGE,"E263.left");Q83=makeQuery(id+"F0.imprint","IMPRINT",FACE,{"disambiguationData":[TD([[makeQuery(id+"F0.imprint","IMPRINT",EDGE,{"derivedFrom":subQ0}),1.0]])]});}
            var Q84;
            {var subQ5=sQuery(id+"F0.wireOp",EDGE,"E270.right");Q84=makeQuery(id+"F0.imprint","IMPRINT",FACE,{"disambiguationData":[TD([[makeQuery(id+"F0.imprint","IMPRINT",EDGE,{"derivedFrom":subQ5}),1.0]])]});}
            var Q85;
            {var subQ0=sQuery(id+"F0.wireOp",EDGE,"E263.right");Q85=makeQuery(id+"F0.imprint","IMPRINT",FACE,{"disambiguationData":[TD([[makeQuery(id+"F0.imprint","IMPRINT",EDGE,{"derivedFrom":subQ0}),1.0]])]});}
            var Q86;
            {var subQ0=sQuery(id+"F0.wireOp",EDGE,"E264.left");Q86=makeQuery(id+"F0.imprint","IMPRINT",FACE,{"disambiguationData":[TD([[makeQuery(id+"F0.imprint","IMPRINT",EDGE,{"derivedFrom":subQ0}),1.0]])]});}
            var Q87;
            {var subQ0=sQuery(id+"F0.wireOp",EDGE,"E264.right");Q87=makeQuery(id+"F0.imprint","IMPRINT",FACE,{"disambiguationData":[TD([[makeQuery(id+"F0.imprint","IMPRINT",EDGE,{"derivedFrom":subQ0}),1.0]])]});}
            var Q88;
            {var subQ0=sQuery(id+"F0.wireOp",EDGE,"E265.left");Q88=makeQuery(id+"F0.imprint","IMPRINT",FACE,{"disambiguationData":[TD([[makeQuery(id+"F0.imprint","IMPRINT",EDGE,{"derivedFrom":subQ0}),1.0]])]});}
            var Q89;
            {var subQ0=sQuery(id+"F0.wireOp",EDGE,"E270.left");Q89=makeQuery(id+"F0.imprint","IMPRINT",FACE,{"disambiguationData":[TD([[makeQuery(id+"F0.imprint","IMPRINT",EDGE,{"derivedFrom":subQ0}),1.0]])]});}
            var Q90;
            {var subQ0=sQuery(id+"F0.wireOp",EDGE,"E270.left");Q90=makeQuery(id+"F0.imprint","IMPRINT",FACE,{"disambiguationData":[TD([[makeQuery(id+"F0.imprint","IMPRINT",EDGE,{"derivedFrom":subQ0}),-1.0]])]});}
            var Q91;
            {var subQ0=sQuery(id+"F0.wireOp",EDGE,"E271.left");Q91=makeQuery(id+"F0.imprint","IMPRINT",FACE,{"disambiguationData":[TD([[makeQuery(id+"F0.imprint","IMPRINT",EDGE,{"derivedFrom":subQ0}),1.0]])]});}
            var Q92;
            {var subQ4=sQuery(id+"F0.wireOp",EDGE,"E271.left");Q92=makeQuery(id+"F0.imprint","IMPRINT",FACE,{"disambiguationData":[TD([[makeQuery(id+"F0.imprint","IMPRINT",EDGE,{"derivedFrom":subQ4}),-1.0]])]});}
            var Q93;
            {var subQ0=sQuery(id+"F0.wireOp",EDGE,"E272.left");Q93=makeQuery(id+"F0.imprint","IMPRINT",FACE,{"disambiguationData":[TD([[makeQuery(id+"F0.imprint","IMPRINT",EDGE,{"derivedFrom":subQ0}),1.0]])]});}
            var Q94;
            {var subQ0=sQuery(id+"F0.wireOp",EDGE,"E272.left");Q94=makeQuery(id+"F0.imprint","IMPRINT",FACE,{"disambiguationData":[TD([[makeQuery(id+"F0.imprint","IMPRINT",EDGE,{"derivedFrom":subQ0}),-1.0]])]});}
            var Q95;
            {var subQ0=sQuery(id+"F0.wireOp",EDGE,"E266.left");Q95=makeQuery(id+"F0.imprint","IMPRINT",FACE,{"disambiguationData":[TD([[makeQuery(id+"F0.imprint","IMPRINT",EDGE,{"derivedFrom":subQ0}),1.0]])]});}
            var Q96;
            {var subQ2=sQuery(id+"F0.wireOp",EDGE,"E266.left");Q96=makeQuery(id+"F0.imprint","IMPRINT",FACE,{"disambiguationData":[TD([[makeQuery(id+"F0.imprint","IMPRINT",EDGE,{"derivedFrom":subQ2}),-1.0]])]});}
            var Q97;
            {var subQ0=sQuery(id+"F0.wireOp",EDGE,"E268.left");Q97=makeQuery(id+"F0.imprint","IMPRINT",FACE,{"disambiguationData":[TD([[makeQuery(id+"F0.imprint","IMPRINT",EDGE,{"derivedFrom":subQ0}),1.0]])]});}
            var Q98;
            {var subQ0=sQuery(id+"F0.wireOp",EDGE,"E273.left");Q98=makeQuery(id+"F0.imprint","IMPRINT",FACE,{"disambiguationData":[TD([[makeQuery(id+"F0.imprint","IMPRINT",EDGE,{"derivedFrom":subQ0}),1.0]])]});}
            var Q99;
            {var subQ0=sQuery(id+"F0.wireOp",EDGE,"E266.right");Q99=makeQuery(id+"F0.imprint","IMPRINT",FACE,{"disambiguationData":[TD([[makeQuery(id+"F0.imprint","IMPRINT",EDGE,{"derivedFrom":subQ0}),1.0]])]});}
            var Q100;
            {var subQ4=sQuery(id+"F0.wireOp",EDGE,"E265.right");Q100=makeQuery(id+"F0.imprint","IMPRINT",FACE,{"disambiguationData":[TD([[makeQuery(id+"F0.imprint","IMPRINT",EDGE,{"derivedFrom":subQ4}),1.0]])]});}
            var Q101;
            {var subQ0=sQuery(id+"F0.wireOp",EDGE,"E269.left");Q101=makeQuery(id+"F0.imprint","IMPRINT",FACE,{"disambiguationData":[TD([[makeQuery(id+"F0.imprint","IMPRINT",EDGE,{"derivedFrom":subQ0}),1.0]])]});}
            var Q102;
            {var subQ0=sQuery(id+"F0.wireOp",EDGE,"E267.left");Q102=makeQuery(id+"F0.imprint","IMPRINT",FACE,{"disambiguationData":[TD([[makeQuery(id+"F0.imprint","IMPRINT",EDGE,{"derivedFrom":subQ0}),-1.0]])]});}
            var Q103;
            {var subQ0=sQuery(id+"F0.wireOp",EDGE,"E267.left");Q103=makeQuery(id+"F0.imprint","IMPRINT",FACE,{"disambiguationData":[TD([[makeQuery(id+"F0.imprint","IMPRINT",EDGE,{"derivedFrom":subQ0}),1.0]])]});}
            var Q104;
            {var subQ3=sQuery(id+"F0.wireOp",EDGE,"E267.right");Q104=makeQuery(id+"F0.imprint","IMPRINT",FACE,{"disambiguationData":[TD([[makeQuery(id+"F0.imprint","IMPRINT",EDGE,{"derivedFrom":subQ3}),1.0]])]});}
            var Q105;
            {var subQ5=sQuery(id+"F0.wireOp",EDGE,"E278.top");Q105=makeQuery(id+"F0.imprint","IMPRINT",FACE,{"disambiguationData":[TD([[makeQuery(id+"F0.imprint","IMPRINT",EDGE,{"derivedFrom":subQ5}),-1.0]])]});}
            var Q106;
            {var subQ0=sQuery(id+"F0.wireOp",EDGE,"E278.bottom");Q106=makeQuery(id+"F0.imprint","IMPRINT",FACE,{"disambiguationData":[TD([[makeQuery(id+"F0.imprint","IMPRINT",EDGE,{"derivedFrom":subQ0}),-1.0]])]});}
            var Q107;
            Q107=makeQuery(id+"F0.imprint","IMPRINT",FACE,{"disambiguationData":[TD([[makeQuery(id+"F0.imprint","IMPRINT",EDGE,{"derivedFrom":sQuery(id+"F0.wireOp",EDGE,"E174")}),1.0]])]});
            var Q108;
            {var subQ0=sQuery(id+"F0.wireOp",EDGE,"E274.bottom");Q108=makeQuery(id+"F0.imprint","IMPRINT",FACE,{"disambiguationData":[TD([[makeQuery(id+"F0.imprint","IMPRINT",EDGE,{"derivedFrom":subQ0}),-1.0]])]});}
            var Q109;
            {var subQ4=sQuery(id+"F0.wireOp",EDGE,"E138.left");Q109=makeQuery(id+"F0.imprint","IMPRINT",FACE,{"disambiguationData":[TD([[makeQuery(id+"F0.imprint","IMPRINT",EDGE,{"derivedFrom":subQ4}),-1.0]])]});}
            var Q110;
            {var subQ2=sQuery(id+"F0.wireOp",EDGE,"E281.left");Q110=makeQuery(id+"F0.imprint","IMPRINT",FACE,{"disambiguationData":[TD([[makeQuery(id+"F0.imprint","IMPRINT",EDGE,{"derivedFrom":subQ2}),1.0]])]});}
            var Q111;
            {var subQ0=sQuery(id+"F0.wireOp",EDGE,"E280.left");Q111=makeQuery(id+"F0.imprint","IMPRINT",FACE,{"disambiguationData":[TD([[makeQuery(id+"F0.imprint","IMPRINT",EDGE,{"derivedFrom":subQ0}),1.0]])]});}
            var Q112;
            {var subQ0=sQuery(id+"F0.wireOp",EDGE,"E279.left");Q112=makeQuery(id+"F0.imprint","IMPRINT",FACE,{"disambiguationData":[TD([[makeQuery(id+"F0.imprint","IMPRINT",EDGE,{"derivedFrom":subQ0}),1.0]])]});}
            var Q113;
            {var subQ5=sQuery(id+"F0.wireOp",EDGE,"E138.right");Q113=makeQuery(id+"F0.imprint","IMPRINT",FACE,{"disambiguationData":[TD([[makeQuery(id+"F0.imprint","IMPRINT",EDGE,{"derivedFrom":subQ5}),1.0]])]});}
            var Q114;
            {var subQ0=sQuery(id+"F0.wireOp",EDGE,"E277.left");Q114=makeQuery(id+"F0.imprint","IMPRINT",FACE,{"disambiguationData":[TD([[makeQuery(id+"F0.imprint","IMPRINT",EDGE,{"derivedFrom":subQ0}),1.0]])]});}
            var Q115;
            {var subQ4=sQuery(id+"F0.wireOp",EDGE,"E276.left");Q115=makeQuery(id+"F0.imprint","IMPRINT",FACE,{"disambiguationData":[TD([[makeQuery(id+"F0.imprint","IMPRINT",EDGE,{"derivedFrom":subQ4}),-1.0]])]});}
            var Q116;
            {var subQ0=sQuery(id+"F0.wireOp",EDGE,"E276.left");Q116=makeQuery(id+"F0.imprint","IMPRINT",FACE,{"disambiguationData":[TD([[makeQuery(id+"F0.imprint","IMPRINT",EDGE,{"derivedFrom":subQ0}),1.0]])]});}
            var Q117;
            {var subQ4=sQuery(id+"F0.wireOp",EDGE,"E275.left");Q117=makeQuery(id+"F0.imprint","IMPRINT",FACE,{"disambiguationData":[TD([[makeQuery(id+"F0.imprint","IMPRINT",EDGE,{"derivedFrom":subQ4}),-1.0]])]});}
            var Q118;
            {var subQ2=sQuery(id+"F0.wireOp",EDGE,"E275.left");Q118=makeQuery(id+"F0.imprint","IMPRINT",FACE,{"disambiguationData":[TD([[makeQuery(id+"F0.imprint","IMPRINT",EDGE,{"derivedFrom":subQ2}),1.0]])]});}
            var Q119;
            {var subQ2=sQuery(id+"F0.wireOp",EDGE,"E283.bottom");Q119=makeQuery(id+"F0.imprint","IMPRINT",FACE,{"disambiguationData":[TD([[makeQuery(id+"F0.imprint","IMPRINT",EDGE,{"derivedFrom":subQ2}),-1.0]])]});}
            var Q120;
            {var subQ0=sQuery(id+"F0.wireOp",EDGE,"E274.top");Q120=makeQuery(id+"F0.imprint","IMPRINT",FACE,{"disambiguationData":[TD([[makeQuery(id+"F0.imprint","IMPRINT",EDGE,{"derivedFrom":subQ0}),-1.0]])]});}
            var Q121;
            {var subQ9=sQuery(id+"F0.wireOp",EDGE,"E278.bottom");Q121=makeQuery(id+"F0.imprint","IMPRINT",FACE,{"disambiguationData":[TD([[makeQuery(id+"F0.imprint","IMPRINT",EDGE,{"derivedFrom":subQ9}),1.0]])]});}
            var Q122;
            {var subQ2=sQuery(id+"F0.wireOp",EDGE,"E282.bottom");Q122=makeQuery(id+"F0.imprint","IMPRINT",FACE,{"disambiguationData":[TD([[makeQuery(id+"F0.imprint","IMPRINT",EDGE,{"derivedFrom":subQ2}),-1.0]])]});}
            var Q123;
            {var subQ7=sQuery(id+"F0.wireOp",EDGE,"E248.trimOffspring");Q123=makeQuery(id+"F0.imprint","IMPRINT",FACE,{"disambiguationData":[TD([[makeQuery(id+"F0.imprint","IMPRINT",EDGE,{"derivedFrom":subQ7}),1.0]])]});}
            var Q124;
            {var subQ2=sQuery(id+"F0.wireOp",EDGE,"E284.bottom");Q124=makeQuery(id+"F0.imprint","IMPRINT",FACE,{"disambiguationData":[TD([[makeQuery(id+"F0.imprint","IMPRINT",EDGE,{"derivedFrom":subQ2}),-1.0]])]});}
            var Q125;
            {var subQ2=sQuery(id+"F0.wireOp",EDGE,"E285.bottom");Q125=makeQuery(id+"F0.imprint","IMPRINT",FACE,{"disambiguationData":[TD([[makeQuery(id+"F0.imprint","IMPRINT",EDGE,{"derivedFrom":subQ2}),-1.0]])]});}
            var Q126;
            {var subQ8=sQuery(id+"F0.wireOp",EDGE,"E49.left");Q126=makeQuery(id+"F0.imprint","IMPRINT",FACE,{"disambiguationData":[TD([[makeQuery(id+"F0.imprint","IMPRINT",EDGE,{"derivedFrom":subQ8}),1.0]])]});}
            extrude(context, id + "F1", {"entities" : qUnion([Q0, Q1, Q2, Q3, Q4, Q5, Q6, Q7, Q8, Q9, Q10, Q11, Q12, Q13, Q14, Q15, Q16, Q17, Q18, Q19, Q20, Q21, Q22, Q23, Q24, Q25, Q26, Q27, Q28, Q29, Q30, Q31, Q32, Q33, Q34, Q35, Q36, Q37, Q38, Q39, Q40, Q41, Q42, Q43, Q44, Q45, Q46, Q47, Q48, Q49, Q50, Q51, Q52, Q53, Q54, Q55, Q56, Q57, Q58, Q59, Q60, Q61, Q62, Q63, Q64, Q65, Q66, Q67, Q68, Q69, Q70, Q71, Q72, Q73, Q74, Q75, Q76, Q77, Q78, Q79, Q80, Q81, Q82, Q83, Q84, Q85, Q86, Q87, Q88, Q89, Q90, Q91, Q92, Q93, Q94, Q95, Q96, Q97, Q98, Q99, Q100, Q101, Q102, Q103, Q104, Q105, Q106, Q107, Q108, Q109, Q110, Q111, Q112, Q113, Q114, Q115, Q116, Q117, Q118, Q119, Q120, Q121, Q122, Q123, Q124, Q125, Q126]), "depth" : 2743.2 * mm, "offsetDistance" : 25.4 * mm});
        }
        {
            var Q0;
            {var subQ3=sQuery(id+"F0.wireOp",EDGE,"E54.right");Q0=makeQuery(id+"F0.imprint","IMPRINT",FACE,{"disambiguationData":[TD([[makeQuery(id+"F0.imprint","IMPRINT",EDGE,{"derivedFrom":subQ3}),1.0]])]});}
            var Q1;
            {var subQ6=sQuery(id+"F0.wireOp",EDGE,"E16.6");Q1=makeQuery(id+"F0.imprint","IMPRINT",FACE,{"disambiguationData":[TD([[makeQuery(id+"F0.imprint","IMPRINT",EDGE,{"derivedFrom":subQ6}),-1.0]])]});}
            var Q2;
            {var subQ0=sQuery(id+"F0.wireOp",EDGE,"E16.8");Q2=makeQuery(id+"F0.imprint","IMPRINT",FACE,{"disambiguationData":[TD([[makeQuery(id+"F0.imprint","IMPRINT",EDGE,{"derivedFrom":subQ0}),-1.0]])]});}
            var Q3;
            {var subQ3=sQuery(id+"F0.wireOp",EDGE,"E16.9");Q3=makeQuery(id+"F0.imprint","IMPRINT",FACE,{"disambiguationData":[TD([[makeQuery(id+"F0.imprint","IMPRINT",EDGE,{"derivedFrom":subQ3}),-1.0]])]});}
            var Q4;
            {var subQ0=sQuery(id+"F0.wireOp",EDGE,"E16.11");Q4=makeQuery(id+"F0.imprint","IMPRINT",FACE,{"disambiguationData":[TD([[makeQuery(id+"F0.imprint","IMPRINT",EDGE,{"derivedFrom":subQ0}),-1.0]])]});}
            var Q5;
            {var subQ1=sQuery(id+"F0.wireOp",EDGE,"E16.13");Q5=makeQuery(id+"F0.imprint","IMPRINT",FACE,{"disambiguationData":[TD([[makeQuery(id+"F0.imprint","IMPRINT",EDGE,{"derivedFrom":subQ1}),-1.0]])]});}
            var Q6;
            {var subQ0=sQuery(id+"F0.wireOp",EDGE,"E56.left");Q6=makeQuery(id+"F0.imprint","IMPRINT",FACE,{"disambiguationData":[TD([[makeQuery(id+"F0.imprint","IMPRINT",EDGE,{"derivedFrom":subQ0}),-1.0]])]});}
            var Q7;
            {var subQ0=sQuery(id+"F0.wireOp",EDGE,"E56.right");Q7=makeQuery(id+"F0.imprint","IMPRINT",FACE,{"disambiguationData":[TD([[makeQuery(id+"F0.imprint","IMPRINT",EDGE,{"derivedFrom":subQ0}),1.0]])]});}
            var Q8;
            Q8=makeQuery(id+"F0.imprint","IMPRINT",FACE,{"disambiguationData":[TD([[makeQuery(id+"F0.imprint","IMPRINT",EDGE,{"derivedFrom":sQuery(id+"F0.wireOp",EDGE,"E175")}),-1.0]])]});
            var Q9;
            {var subQ0=sQuery(id+"F0.wireOp",EDGE,"E49.right");Q9=makeQuery(id+"F0.imprint","IMPRINT",FACE,{"disambiguationData":[TD([[makeQuery(id+"F0.imprint","IMPRINT",EDGE,{"derivedFrom":subQ0}),1.0]])]});}
            var Q10;
            {var subQ1=sQuery(id+"F0.wireOp",EDGE,"E16.4");Q10=makeQuery(id+"F0.imprint","IMPRINT",FACE,{"disambiguationData":[TD([[makeQuery(id+"F0.imprint","IMPRINT",EDGE,{"derivedFrom":subQ1}),-1.0]])]});}
            var Q11;
            {var subQ0=sQuery(id+"F0.wireOp",EDGE,"E17.bottom");Q11=makeQuery(id+"F0.imprint","IMPRINT",FACE,{"disambiguationData":[TD([[makeQuery(id+"F0.imprint","IMPRINT",EDGE,{"derivedFrom":subQ0}),1.0]])]});}
            var Q12;
            {var subQ5=sQuery(id+"F0.wireOp",EDGE,"E17.top");Q12=makeQuery(id+"F0.imprint","IMPRINT",FACE,{"disambiguationData":[TD([[makeQuery(id+"F0.imprint","IMPRINT",EDGE,{"derivedFrom":subQ5}),-1.0]])]});}
            var Q13;
            {var subQ0=sQuery(id+"F0.wireOp",EDGE,"E118.top");Q13=makeQuery(id+"F0.imprint","IMPRINT",FACE,{"disambiguationData":[TD([[makeQuery(id+"F0.imprint","IMPRINT",EDGE,{"derivedFrom":subQ0}),-1.0]])]});}
            var Q14;
            {var subQ6=sQuery(id+"F0.wireOp",EDGE,"E103.top");Q14=makeQuery(id+"F0.imprint","IMPRINT",FACE,{"disambiguationData":[TD([[makeQuery(id+"F0.imprint","IMPRINT",EDGE,{"derivedFrom":subQ6}),-1.0]])]});}
            var Q15;
            {var subQ27=sQuery(id+"F0.wireOp",EDGE,"E93");Q15=makeQuery(id+"F0.imprint","IMPRINT",FACE,{"disambiguationData":[TD([[makeQuery(id+"F0.imprint","IMPRINT",EDGE,{"derivedFrom":subQ27}),1.0]])]});}
            var Q16;
            {var subQ0=sQuery(id+"F0.wireOp",EDGE,"E140");Q16=makeQuery(id+"F0.imprint","IMPRINT",FACE,{"disambiguationData":[TD([[makeQuery(id+"F0.imprint","IMPRINT",EDGE,{"derivedFrom":subQ0}),1.0]])]});}
            var Q17;
            {var subQ4=sQuery(id+"F0.wireOp",EDGE,"E141");Q17=makeQuery(id+"F0.imprint","IMPRINT",FACE,{"disambiguationData":[TD([[makeQuery(id+"F0.imprint","IMPRINT",EDGE,{"derivedFrom":subQ4}),-1.0]])]});}
            var Q18;
            {var subQ4=sQuery(id+"F0.wireOp",EDGE,"E143");Q18=makeQuery(id+"F0.imprint","IMPRINT",FACE,{"disambiguationData":[TD([[makeQuery(id+"F0.imprint","IMPRINT",EDGE,{"derivedFrom":subQ4}),-1.0]])]});}
            var Q19;
            {var subQ2=sQuery(id+"F0.wireOp",EDGE,"E144");Q19=makeQuery(id+"F0.imprint","IMPRINT",FACE,{"disambiguationData":[TD([[makeQuery(id+"F0.imprint","IMPRINT",EDGE,{"derivedFrom":subQ2}),-1.0]])]});}
            var Q20;
            {var subQ6=sQuery(id+"F0.wireOp",EDGE,"E151.trimOffspring");Q20=makeQuery(id+"F0.imprint","IMPRINT",FACE,{"disambiguationData":[TD([[makeQuery(id+"F0.imprint","IMPRINT",EDGE,{"derivedFrom":subQ6}),-1.0]])]});}
            var Q21;
            {var subQ6=sQuery(id+"F0.wireOp",EDGE,"E145");Q21=makeQuery(id+"F0.imprint","IMPRINT",FACE,{"disambiguationData":[TD([[makeQuery(id+"F0.imprint","IMPRINT",EDGE,{"derivedFrom":subQ6}),-1.0]])]});}
            var Q22;
            {var subQ3=sQuery(id+"F0.wireOp",EDGE,"E137.3");Q22=makeQuery(id+"F0.imprint","IMPRINT",FACE,{"disambiguationData":[TD([[makeQuery(id+"F0.imprint","IMPRINT",EDGE,{"derivedFrom":subQ3}),-1.0]])]});}
            var Q23;
            {var subQ1=sQuery(id+"F0.wireOp",EDGE,"E136.bottom");Q23=makeQuery(id+"F0.imprint","IMPRINT",FACE,{"disambiguationData":[TD([[makeQuery(id+"F0.imprint","IMPRINT",EDGE,{"derivedFrom":subQ1}),-1.0]])]});}
            var Q24;
            {var subQ0=sQuery(id+"F0.wireOp",EDGE,"E90.right");Q24=makeQuery(id+"F0.imprint","IMPRINT",FACE,{"disambiguationData":[TD([[makeQuery(id+"F0.imprint","IMPRINT",EDGE,{"derivedFrom":subQ0}),1.0]])]});}
            var Q25;
            {var subQ2=sQuery(id+"F0.wireOp",EDGE,"E191");Q25=makeQuery(id+"F0.imprint","IMPRINT",FACE,{"disambiguationData":[TD([[makeQuery(id+"F0.imprint","IMPRINT",EDGE,{"derivedFrom":subQ2}),-1.0]])]});}
            var Q26;
            {var subQ5=sQuery(id+"F0.wireOp",EDGE,"E185");Q26=makeQuery(id+"F0.imprint","IMPRINT",FACE,{"disambiguationData":[TD([[makeQuery(id+"F0.imprint","IMPRINT",EDGE,{"derivedFrom":subQ5}),-1.0]])]});}
            var Q27;
            {var subQ10=sQuery(id+"F0.wireOp",EDGE,"E179");Q27=makeQuery(id+"F0.imprint","IMPRINT",FACE,{"disambiguationData":[TD([[makeQuery(id+"F0.imprint","IMPRINT",EDGE,{"derivedFrom":subQ10}),-1.0]])]});}
            var Q28;
            {var subQ6=sQuery(id+"F0.wireOp",EDGE,"E248.trimOffspring");Q28=makeQuery(id+"F0.imprint","IMPRINT",FACE,{"disambiguationData":[TD([[makeQuery(id+"F0.imprint","IMPRINT",EDGE,{"derivedFrom":subQ6}),-1.0]])]});}
            var Q29;
            {var subQ0=sQuery(id+"F0.wireOp",EDGE,"E257");Q29=makeQuery(id+"F0.imprint","IMPRINT",FACE,{"disambiguationData":[TD([[makeQuery(id+"F0.imprint","IMPRINT",EDGE,{"derivedFrom":subQ0}),1.0]])]});}
            var Q30;
            {var subQ1=sQuery(id+"F0.wireOp",EDGE,"E256");Q30=makeQuery(id+"F0.imprint","IMPRINT",FACE,{"disambiguationData":[TD([[makeQuery(id+"F0.imprint","IMPRINT",EDGE,{"derivedFrom":subQ1}),1.0]])]});}
            var Q31;
            {var subQ0=sQuery(id+"F0.wireOp",EDGE,"E263.left");Q31=makeQuery(id+"F0.imprint","IMPRINT",FACE,{"disambiguationData":[TD([[makeQuery(id+"F0.imprint","IMPRINT",EDGE,{"derivedFrom":subQ0}),1.0]])]});}
            var Q32;
            {var subQ1=sQuery(id+"F0.wireOp",EDGE,"E114.left");Q32=makeQuery(id+"F0.imprint","IMPRINT",FACE,{"disambiguationData":[TD([[makeQuery(id+"F0.imprint","IMPRINT",EDGE,{"derivedFrom":subQ1}),-1.0]])]});}
            var Q33;
            {var subQ4=sQuery(id+"F0.wireOp",EDGE,"E166.left");Q33=makeQuery(id+"F0.imprint","IMPRINT",FACE,{"disambiguationData":[TD([[makeQuery(id+"F0.imprint","IMPRINT",EDGE,{"derivedFrom":subQ4}),-1.0]])]});}
            var Q34;
            {var subQ0=sQuery(id+"F0.wireOp",EDGE,"E264.left");Q34=makeQuery(id+"F0.imprint","IMPRINT",FACE,{"disambiguationData":[TD([[makeQuery(id+"F0.imprint","IMPRINT",EDGE,{"derivedFrom":subQ0}),1.0]])]});}
            var Q35;
            {var subQ0=sQuery(id+"F0.wireOp",EDGE,"E265.left");Q35=makeQuery(id+"F0.imprint","IMPRINT",FACE,{"disambiguationData":[TD([[makeQuery(id+"F0.imprint","IMPRINT",EDGE,{"derivedFrom":subQ0}),1.0]])]});}
            var Q36;
            {var subQ0=sQuery(id+"F0.wireOp",EDGE,"E266.left");Q36=makeQuery(id+"F0.imprint","IMPRINT",FACE,{"disambiguationData":[TD([[makeQuery(id+"F0.imprint","IMPRINT",EDGE,{"derivedFrom":subQ0}),1.0]])]});}
            var Q37;
            {var subQ0=sQuery(id+"F0.wireOp",EDGE,"E267.left");Q37=makeQuery(id+"F0.imprint","IMPRINT",FACE,{"disambiguationData":[TD([[makeQuery(id+"F0.imprint","IMPRINT",EDGE,{"derivedFrom":subQ0}),1.0]])]});}
            var Q38;
            {var subQ4=sQuery(id+"F0.wireOp",EDGE,"E67.left");Q38=makeQuery(id+"F0.imprint","IMPRINT",FACE,{"disambiguationData":[TD([[makeQuery(id+"F0.imprint","IMPRINT",EDGE,{"derivedFrom":subQ4}),-1.0]])]});}
            var Q39;
            {var subQ0=sQuery(id+"F0.wireOp",EDGE,"E82.right");Q39=makeQuery(id+"F0.imprint","IMPRINT",FACE,{"disambiguationData":[TD([[makeQuery(id+"F0.imprint","IMPRINT",EDGE,{"derivedFrom":subQ0}),1.0]])]});}
            var Q40;
            {var subQ0=sQuery(id+"F0.wireOp",EDGE,"E56.left");Q40=makeQuery(id+"F0.imprint","IMPRINT",FACE,{"disambiguationData":[TD([[makeQuery(id+"F0.imprint","IMPRINT",EDGE,{"derivedFrom":subQ0}),1.0]])]});}
            var Q41;
            {var subQ0=sQuery(id+"F0.wireOp",EDGE,"E103.left");Q41=makeQuery(id+"F0.imprint","IMPRINT",FACE,{"disambiguationData":[TD([[makeQuery(id+"F0.imprint","IMPRINT",EDGE,{"derivedFrom":subQ0}),-1.0]])]});}
            var Q42;
            {var subQ2=sQuery(id+"F0.wireOp",EDGE,"E54.left");Q42=makeQuery(id+"F0.imprint","IMPRINT",FACE,{"disambiguationData":[TD([[makeQuery(id+"F0.imprint","IMPRINT",EDGE,{"derivedFrom":subQ2}),1.0]])]});}
            var Q43;
            {var subQ5=sQuery(id+"F0.wireOp",EDGE,"E140");Q43=makeQuery(id+"F0.imprint","IMPRINT",FACE,{"disambiguationData":[TD([[makeQuery(id+"F0.imprint","IMPRINT",EDGE,{"derivedFrom":subQ5}),-1.0]])]});}
            var Q44;
            {var subQ0=sQuery(id+"F0.wireOp",EDGE,"E103.right");Q44=makeQuery(id+"F0.imprint","IMPRINT",FACE,{"disambiguationData":[TD([[makeQuery(id+"F0.imprint","IMPRINT",EDGE,{"derivedFrom":subQ0}),1.0]])]});}
            var Q45;
            {var subQ0=sQuery(id+"F0.wireOp",EDGE,"E55.left");Q45=makeQuery(id+"F0.imprint","IMPRINT",FACE,{"disambiguationData":[TD([[makeQuery(id+"F0.imprint","IMPRINT",EDGE,{"derivedFrom":subQ0}),1.0]])]});}
            var Q46;
            {var subQ11=sQuery(id+"F0.wireOp",EDGE,"E7");Q46=makeQuery(id+"F0.imprint","IMPRINT",FACE,{"disambiguationData":[TD([[makeQuery(id+"F0.imprint","IMPRINT",EDGE,{"derivedFrom":subQ11}),-1.0]])]});}
            var Q47;
            {var subQ7=sQuery(id+"F0.wireOp",EDGE,"E178");Q47=makeQuery(id+"F0.imprint","IMPRINT",FACE,{"disambiguationData":[TD([[makeQuery(id+"F0.imprint","IMPRINT",EDGE,{"derivedFrom":subQ7}),-1.0]])]});}
            var Q48;
            {var subQ1=sQuery(id+"F0.wireOp",EDGE,"E11");Q48=makeQuery(id+"F0.imprint","IMPRINT",FACE,{"disambiguationData":[TD([[makeQuery(id+"F0.imprint","IMPRINT",EDGE,{"derivedFrom":subQ1}),-1.0]])]});}
            var Q49;
            {var subQ4=sQuery(id+"F0.wireOp",EDGE,"E280.right");Q49=makeQuery(id+"F0.imprint","IMPRINT",FACE,{"disambiguationData":[TD([[makeQuery(id+"F0.imprint","IMPRINT",EDGE,{"derivedFrom":subQ4}),1.0]])]});}
            var Q50;
            {var subQ2=sQuery(id+"F0.wireOp",EDGE,"E279.right");Q50=makeQuery(id+"F0.imprint","IMPRINT",FACE,{"disambiguationData":[TD([[makeQuery(id+"F0.imprint","IMPRINT",EDGE,{"derivedFrom":subQ2}),1.0]])]});}
            var Q51;
            {var subQ2=sQuery(id+"F0.wireOp",EDGE,"E60.left");Q51=makeQuery(id+"F0.imprint","IMPRINT",FACE,{"disambiguationData":[TD([[makeQuery(id+"F0.imprint","IMPRINT",EDGE,{"derivedFrom":subQ2}),1.0]])]});}
            var Q52;
            {var subQ2=sQuery(id+"F0.wireOp",EDGE,"E90.left");Q52=makeQuery(id+"F0.imprint","IMPRINT",FACE,{"disambiguationData":[TD([[makeQuery(id+"F0.imprint","IMPRINT",EDGE,{"derivedFrom":subQ2}),1.0]])]});}
            var Q53;
            {var subQ4=sQuery(id+"F0.wireOp",EDGE,"E82.left");Q53=makeQuery(id+"F0.imprint","IMPRINT",FACE,{"disambiguationData":[TD([[makeQuery(id+"F0.imprint","IMPRINT",EDGE,{"derivedFrom":subQ4}),-1.0]])]});}
            var Q54;
            {var subQ4=sQuery(id+"F0.wireOp",EDGE,"E154.left");Q54=makeQuery(id+"F0.imprint","IMPRINT",FACE,{"disambiguationData":[TD([[makeQuery(id+"F0.imprint","IMPRINT",EDGE,{"derivedFrom":subQ4}),-1.0]])]});}
            var Q55;
            {var subQ3=sQuery(id+"F0.wireOp",EDGE,"E79.right");Q55=makeQuery(id+"F0.imprint","IMPRINT",FACE,{"disambiguationData":[TD([[makeQuery(id+"F0.imprint","IMPRINT",EDGE,{"derivedFrom":subQ3}),1.0]])]});}
            var Q56;
            {var subQ1=sQuery(id+"F0.wireOp",EDGE,"E195");var subQ3=sQuery(id+"F0.wireOp",EDGE,"E240");var subQ4=makeQuery(id+"F0.imprint","INTERSECT",VERTEX,{"derivedFrom":[subQ1,subQ3]});Q56=makeQuery(id+"F0.imprint","IMPRINT",FACE,{"disambiguationData":[TD([[makeQuery(id+"F0.imprint","IMPRINT",EDGE,{"disambiguationData":[TD([[subQ4,1.0]])],"derivedFrom":subQ3}),1.0]])]});}
            var Q57;
            {var subQ4=sQuery(id+"F0.wireOp",EDGE,"E162.left");Q57=makeQuery(id+"F0.imprint","IMPRINT",FACE,{"disambiguationData":[TD([[makeQuery(id+"F0.imprint","IMPRINT",EDGE,{"derivedFrom":subQ4}),-1.0]])]});}
            var Q58;
            {var subQ5=sQuery(id+"F0.wireOp",EDGE,"E17.bottom");Q58=makeQuery(id+"F0.imprint","IMPRINT",FACE,{"disambiguationData":[TD([[makeQuery(id+"F0.imprint","IMPRINT",EDGE,{"derivedFrom":subQ5}),-1.0]])]});}
            var Q59;
            {var subQ0=sQuery(id+"F0.wireOp",EDGE,"E136.top");Q59=makeQuery(id+"F0.imprint","IMPRINT",FACE,{"disambiguationData":[TD([[makeQuery(id+"F0.imprint","IMPRINT",EDGE,{"derivedFrom":subQ0}),-1.0]])]});}
            var Q60;
            {var subQ2=sQuery(id+"F0.wireOp",EDGE,"E136.bottom");Q60=makeQuery(id+"F0.imprint","IMPRINT",FACE,{"disambiguationData":[TD([[makeQuery(id+"F0.imprint","IMPRINT",EDGE,{"derivedFrom":subQ2}),1.0]])]});}
            var Q61;
            {var subQ3=sQuery(id+"F0.wireOp",EDGE,"E176");Q61=makeQuery(id+"F0.imprint","IMPRINT",FACE,{"disambiguationData":[TD([[makeQuery(id+"F0.imprint","IMPRINT",EDGE,{"derivedFrom":subQ3}),-1.0]])]});}
            var Q62;
            {var subQ4=sQuery(id+"F0.wireOp",EDGE,"E63.left");Q62=makeQuery(id+"F0.imprint","IMPRINT",FACE,{"disambiguationData":[TD([[makeQuery(id+"F0.imprint","IMPRINT",EDGE,{"derivedFrom":subQ4}),-1.0]])]});}
            var Q63;
            {var subQ0=sQuery(id+"F0.wireOp",EDGE,"E254");Q63=makeQuery(id+"F0.imprint","IMPRINT",FACE,{"disambiguationData":[TD([[makeQuery(id+"F0.imprint","IMPRINT",EDGE,{"derivedFrom":subQ0}),-1.0]])]});}
            var Q64;
            {var subQ5=sQuery(id+"F0.wireOp",EDGE,"E270.right");Q64=makeQuery(id+"F0.imprint","IMPRINT",FACE,{"disambiguationData":[TD([[makeQuery(id+"F0.imprint","IMPRINT",EDGE,{"derivedFrom":subQ5}),1.0]])]});}
            var Q65;
            {var subQ2=sQuery(id+"F0.wireOp",EDGE,"E50.left");Q65=makeQuery(id+"F0.imprint","IMPRINT",FACE,{"disambiguationData":[TD([[makeQuery(id+"F0.imprint","IMPRINT",EDGE,{"derivedFrom":subQ2}),1.0]])]});}
            var Q66;
            {var subQ4=sQuery(id+"F0.wireOp",EDGE,"E237");Q66=makeQuery(id+"F0.imprint","IMPRINT",FACE,{"disambiguationData":[TD([[makeQuery(id+"F0.imprint","IMPRINT",EDGE,{"derivedFrom":subQ4}),1.0]])]});}
            var Q67;
            {var subQ2=sQuery(id+"F0.wireOp",EDGE,"E51.left");Q67=makeQuery(id+"F0.imprint","IMPRINT",FACE,{"disambiguationData":[TD([[makeQuery(id+"F0.imprint","IMPRINT",EDGE,{"derivedFrom":subQ2}),1.0]])]});}
            var Q68;
            {var subQ4=sQuery(id+"F0.wireOp",EDGE,"E1");Q68=makeQuery(id+"F0.imprint","IMPRINT",FACE,{"disambiguationData":[TD([[makeQuery(id+"F0.imprint","IMPRINT",EDGE,{"derivedFrom":subQ4}),-1.0]])]});}
            var Q69;
            {var subQ5=sQuery(id+"F0.wireOp",EDGE,"E107.right");Q69=makeQuery(id+"F0.imprint","IMPRINT",FACE,{"disambiguationData":[TD([[makeQuery(id+"F0.imprint","IMPRINT",EDGE,{"derivedFrom":subQ5}),1.0]])]});}
            var Q70;
            {var subQ4=sQuery(id+"F0.wireOp",EDGE,"E231.left");Q70=makeQuery(id+"F0.imprint","IMPRINT",FACE,{"disambiguationData":[TD([[makeQuery(id+"F0.imprint","IMPRINT",EDGE,{"derivedFrom":subQ4}),-1.0]])]});}
            var Q71;
            {var subQ3=sQuery(id+"F0.wireOp",EDGE,"E184");Q71=makeQuery(id+"F0.imprint","IMPRINT",FACE,{"disambiguationData":[TD([[makeQuery(id+"F0.imprint","IMPRINT",EDGE,{"derivedFrom":subQ3}),-1.0]])]});}
            var Q72;
            {var subQ2=sQuery(id+"F0.wireOp",EDGE,"E53.left");Q72=makeQuery(id+"F0.imprint","IMPRINT",FACE,{"disambiguationData":[TD([[makeQuery(id+"F0.imprint","IMPRINT",EDGE,{"derivedFrom":subQ2}),1.0]])]});}
            var Q73;
            {var subQ3=sQuery(id+"F0.wireOp",EDGE,"E3");Q73=makeQuery(id+"F0.imprint","IMPRINT",FACE,{"disambiguationData":[TD([[makeQuery(id+"F0.imprint","IMPRINT",EDGE,{"derivedFrom":subQ3}),-1.0]])]});}
            var Q74;
            {var subQ1=sQuery(id+"F0.wireOp",EDGE,"E236");var subQ5=makeQuery(id+"F0.imprint","INTERSECT",VERTEX,{"derivedFrom":[subQ1,sQuery(id+"F0.wireOp",EDGE,"E256")]});Q74=makeQuery(id+"F0.imprint","IMPRINT",FACE,{"disambiguationData":[TD([[makeQuery(id+"F0.imprint","IMPRINT",EDGE,{"disambiguationData":[TD([[subQ5,-1.0]])],"derivedFrom":subQ1}),1.0]])]});}
            var Q75;
            Q75=makeQuery(id+"F0.imprint","IMPRINT",FACE,{"disambiguationData":[TD([[makeQuery(id+"F0.imprint","IMPRINT",EDGE,{"derivedFrom":sQuery(id+"F0.wireOp",EDGE,"E107.bottom")}),-1.0]])]});
            var Q76;
            {var subQ0=sQuery(id+"F0.wireOp",EDGE,"E213.left");Q76=makeQuery(id+"F0.imprint","IMPRINT",FACE,{"disambiguationData":[TD([[makeQuery(id+"F0.imprint","IMPRINT",EDGE,{"derivedFrom":subQ0}),1.0]])]});}
            var Q77;
            {var subQ2=sQuery(id+"F0.wireOp",EDGE,"E202.left");Q77=makeQuery(id+"F0.imprint","IMPRINT",FACE,{"disambiguationData":[TD([[makeQuery(id+"F0.imprint","IMPRINT",EDGE,{"derivedFrom":subQ2}),1.0]])]});}
            var Q78;
            {var subQ2=sQuery(id+"F0.wireOp",EDGE,"E204.left");Q78=makeQuery(id+"F0.imprint","IMPRINT",FACE,{"disambiguationData":[TD([[makeQuery(id+"F0.imprint","IMPRINT",EDGE,{"derivedFrom":subQ2}),1.0]])]});}
            var Q79;
            {var subQ2=sQuery(id+"F0.wireOp",EDGE,"E215.left");Q79=makeQuery(id+"F0.imprint","IMPRINT",FACE,{"disambiguationData":[TD([[makeQuery(id+"F0.imprint","IMPRINT",EDGE,{"derivedFrom":subQ2}),1.0]])]});}
            var Q80;
            {var subQ2=sQuery(id+"F0.wireOp",EDGE,"E57.left");Q80=makeQuery(id+"F0.imprint","IMPRINT",FACE,{"disambiguationData":[TD([[makeQuery(id+"F0.imprint","IMPRINT",EDGE,{"derivedFrom":subQ2}),1.0]])]});}
            var Q81;
            Q81=makeQuery(id+"F0.imprint","IMPRINT",FACE,{"disambiguationData":[TD([[makeQuery(id+"F0.imprint","IMPRINT",EDGE,{"derivedFrom":sQuery(id+"F0.wireOp",EDGE,"E114.bottom")}),-1.0]])]});
            var Q82;
            {var subQ2=sQuery(id+"F0.wireOp",EDGE,"E221.left");Q82=makeQuery(id+"F0.imprint","IMPRINT",FACE,{"disambiguationData":[TD([[makeQuery(id+"F0.imprint","IMPRINT",EDGE,{"derivedFrom":subQ2}),1.0]])]});}
            var Q83;
            {var subQ2=sQuery(id+"F0.wireOp",EDGE,"E223.left");Q83=makeQuery(id+"F0.imprint","IMPRINT",FACE,{"disambiguationData":[TD([[makeQuery(id+"F0.imprint","IMPRINT",EDGE,{"derivedFrom":subQ2}),1.0]])]});}
            var Q84;
            {var subQ0=sQuery(id+"F0.wireOp",EDGE,"E122");Q84=makeQuery(id+"F0.imprint","IMPRINT",FACE,{"disambiguationData":[TD([[makeQuery(id+"F0.imprint","IMPRINT",EDGE,{"derivedFrom":subQ0}),1.0]])]});}
            var Q85;
            {var subQ0=sQuery(id+"F0.wireOp",EDGE,"E154.left");Q85=makeQuery(id+"F0.imprint","IMPRINT",FACE,{"disambiguationData":[TD([[makeQuery(id+"F0.imprint","IMPRINT",EDGE,{"derivedFrom":subQ0}),1.0]])]});}
            var Q86;
            {var subQ2=sQuery(id+"F0.wireOp",EDGE,"E133");Q86=makeQuery(id+"F0.imprint","IMPRINT",FACE,{"disambiguationData":[TD([[makeQuery(id+"F0.imprint","IMPRINT",EDGE,{"derivedFrom":subQ2}),1.0]])]});}
            var Q87;
            {var subQ0=sQuery(id+"F0.wireOp",EDGE,"E190");Q87=makeQuery(id+"F0.imprint","IMPRINT",FACE,{"disambiguationData":[TD([[makeQuery(id+"F0.imprint","IMPRINT",EDGE,{"derivedFrom":subQ0}),-1.0]])]});}
            var Q88;
            {var subQ0=sQuery(id+"F0.wireOp",EDGE,"E158.left");Q88=makeQuery(id+"F0.imprint","IMPRINT",FACE,{"disambiguationData":[TD([[makeQuery(id+"F0.imprint","IMPRINT",EDGE,{"derivedFrom":subQ0}),1.0]])]});}
            var Q89;
            {var subQ2=sQuery(id+"F0.wireOp",EDGE,"E162.left");Q89=makeQuery(id+"F0.imprint","IMPRINT",FACE,{"disambiguationData":[TD([[makeQuery(id+"F0.imprint","IMPRINT",EDGE,{"derivedFrom":subQ2}),1.0]])]});}
            var Q90;
            {var subQ0=sQuery(id+"F0.wireOp",EDGE,"E166.left");Q90=makeQuery(id+"F0.imprint","IMPRINT",FACE,{"disambiguationData":[TD([[makeQuery(id+"F0.imprint","IMPRINT",EDGE,{"derivedFrom":subQ0}),1.0]])]});}
            var Q91;
            {var subQ0=sQuery(id+"F0.wireOp",EDGE,"E221.right");Q91=makeQuery(id+"F0.imprint","IMPRINT",FACE,{"disambiguationData":[TD([[makeQuery(id+"F0.imprint","IMPRINT",EDGE,{"derivedFrom":subQ0}),1.0]])]});}
            var Q92;
            {var subQ2=sQuery(id+"F0.wireOp",EDGE,"E79.left");Q92=makeQuery(id+"F0.imprint","IMPRINT",FACE,{"disambiguationData":[TD([[makeQuery(id+"F0.imprint","IMPRINT",EDGE,{"derivedFrom":subQ2}),-1.0]])]});}
            var Q93;
            {var subQ0=sQuery(id+"F0.wireOp",EDGE,"E202.right");Q93=makeQuery(id+"F0.imprint","IMPRINT",FACE,{"disambiguationData":[TD([[makeQuery(id+"F0.imprint","IMPRINT",EDGE,{"derivedFrom":subQ0}),1.0]])]});}
            var Q94;
            {var subQ0=sQuery(id+"F0.wireOp",EDGE,"E213.right");Q94=makeQuery(id+"F0.imprint","IMPRINT",FACE,{"disambiguationData":[TD([[makeQuery(id+"F0.imprint","IMPRINT",EDGE,{"derivedFrom":subQ0}),1.0]])]});}
            var Q95;
            {var subQ2=sQuery(id+"F0.wireOp",EDGE,"E52.left");Q95=makeQuery(id+"F0.imprint","IMPRINT",FACE,{"disambiguationData":[TD([[makeQuery(id+"F0.imprint","IMPRINT",EDGE,{"derivedFrom":subQ2}),1.0]])]});}
            var Q96;
            Q96=makeQuery(id+"F0.imprint","IMPRINT",FACE,{"disambiguationData":[TD([[makeQuery(id+"F0.imprint","IMPRINT",EDGE,{"derivedFrom":sQuery(id+"F0.wireOp",EDGE,"E103.bottom")}),-1.0]])]});
            var Q97;
            {var subQ0=sQuery(id+"F0.wireOp",EDGE,"E61.left");Q97=makeQuery(id+"F0.imprint","IMPRINT",FACE,{"disambiguationData":[TD([[makeQuery(id+"F0.imprint","IMPRINT",EDGE,{"derivedFrom":subQ0}),1.0]])]});}
            var Q98;
            {var subQ2=sQuery(id+"F0.wireOp",EDGE,"E75.right");Q98=makeQuery(id+"F0.imprint","IMPRINT",FACE,{"disambiguationData":[TD([[makeQuery(id+"F0.imprint","IMPRINT",EDGE,{"derivedFrom":subQ2}),1.0]])]});}
            var Q99;
            {var subQ3=sQuery(id+"F0.wireOp",EDGE,"E71.right");Q99=makeQuery(id+"F0.imprint","IMPRINT",FACE,{"disambiguationData":[TD([[makeQuery(id+"F0.imprint","IMPRINT",EDGE,{"derivedFrom":subQ3}),1.0]])]});}
            var Q100;
            {var subQ0=sQuery(id+"F0.wireOp",EDGE,"E63.left");Q100=makeQuery(id+"F0.imprint","IMPRINT",FACE,{"disambiguationData":[TD([[makeQuery(id+"F0.imprint","IMPRINT",EDGE,{"derivedFrom":subQ0}),1.0]])]});}
            var Q101;
            {var subQ0=sQuery(id+"F0.wireOp",EDGE,"E111.left");Q101=makeQuery(id+"F0.imprint","IMPRINT",FACE,{"disambiguationData":[TD([[makeQuery(id+"F0.imprint","IMPRINT",EDGE,{"derivedFrom":subQ0}),1.0]])]});}
            var Q102;
            {var subQ0=sQuery(id+"F0.wireOp",EDGE,"E65.left");Q102=makeQuery(id+"F0.imprint","IMPRINT",FACE,{"disambiguationData":[TD([[makeQuery(id+"F0.imprint","IMPRINT",EDGE,{"derivedFrom":subQ0}),1.0]])]});}
            var Q103;
            {var subQ2=sQuery(id+"F0.wireOp",EDGE,"E67.left");Q103=makeQuery(id+"F0.imprint","IMPRINT",FACE,{"disambiguationData":[TD([[makeQuery(id+"F0.imprint","IMPRINT",EDGE,{"derivedFrom":subQ2}),1.0]])]});}
            var Q104;
            Q104=makeQuery(id+"F0.imprint","IMPRINT",FACE,{"disambiguationData":[TD([[makeQuery(id+"F0.imprint","IMPRINT",EDGE,{"derivedFrom":sQuery(id+"F0.wireOp",EDGE,"E118.bottom")}),-1.0]])]});
            var Q105;
            {var subQ0=sQuery(id+"F0.wireOp",EDGE,"E228.left");Q105=makeQuery(id+"F0.imprint","IMPRINT",FACE,{"disambiguationData":[TD([[makeQuery(id+"F0.imprint","IMPRINT",EDGE,{"derivedFrom":subQ0}),1.0]])]});}
            var Q106;
            {var subQ0=sQuery(id+"F0.wireOp",EDGE,"E231.left");Q106=makeQuery(id+"F0.imprint","IMPRINT",FACE,{"disambiguationData":[TD([[makeQuery(id+"F0.imprint","IMPRINT",EDGE,{"derivedFrom":subQ0}),1.0]])]});}
            var Q107;
            {var subQ0=sQuery(id+"F0.wireOp",EDGE,"E73.left");Q107=makeQuery(id+"F0.imprint","IMPRINT",FACE,{"disambiguationData":[TD([[makeQuery(id+"F0.imprint","IMPRINT",EDGE,{"derivedFrom":subQ0}),1.0]])]});}
            var Q108;
            {var subQ2=sQuery(id+"F0.wireOp",EDGE,"E234.left");Q108=makeQuery(id+"F0.imprint","IMPRINT",FACE,{"disambiguationData":[TD([[makeQuery(id+"F0.imprint","IMPRINT",EDGE,{"derivedFrom":subQ2}),1.0]])]});}
            var Q109;
            {var subQ2=sQuery(id+"F0.wireOp",EDGE,"E158.left");Q109=makeQuery(id+"F0.imprint","IMPRINT",FACE,{"disambiguationData":[TD([[makeQuery(id+"F0.imprint","IMPRINT",EDGE,{"derivedFrom":subQ2}),-1.0]])]});}
            var Q110;
            {var subQ0=sQuery(id+"F0.wireOp",EDGE,"E75.left");Q110=makeQuery(id+"F0.imprint","IMPRINT",FACE,{"disambiguationData":[TD([[makeQuery(id+"F0.imprint","IMPRINT",EDGE,{"derivedFrom":subQ0}),1.0]])]});}
            var Q111;
            Q111=makeQuery(id+"F0.imprint","IMPRINT",FACE,{"disambiguationData":[TD([[makeQuery(id+"F0.imprint","IMPRINT",EDGE,{"derivedFrom":sQuery(id+"F0.wireOp",EDGE,"E79.bottom")}),-1.0]])]});
            var Q112;
            {var subQ0=sQuery(id+"F0.wireOp",EDGE,"E82.left");Q112=makeQuery(id+"F0.imprint","IMPRINT",FACE,{"disambiguationData":[TD([[makeQuery(id+"F0.imprint","IMPRINT",EDGE,{"derivedFrom":subQ0}),1.0]])]});}
            var Q113;
            {var subQ3=sQuery(id+"F0.wireOp",EDGE,"E63.right");Q113=makeQuery(id+"F0.imprint","IMPRINT",FACE,{"disambiguationData":[TD([[makeQuery(id+"F0.imprint","IMPRINT",EDGE,{"derivedFrom":subQ3}),1.0]])]});}
            var Q114;
            {var subQ2=sQuery(id+"F0.wireOp",EDGE,"E84.left");Q114=makeQuery(id+"F0.imprint","IMPRINT",FACE,{"disambiguationData":[TD([[makeQuery(id+"F0.imprint","IMPRINT",EDGE,{"derivedFrom":subQ2}),1.0]])]});}
            var Q115;
            {var subQ0=sQuery(id+"F0.wireOp",EDGE,"E86.left");Q115=makeQuery(id+"F0.imprint","IMPRINT",FACE,{"disambiguationData":[TD([[makeQuery(id+"F0.imprint","IMPRINT",EDGE,{"derivedFrom":subQ0}),1.0]])]});}
            var Q116;
            {var subQ3=sQuery(id+"F0.wireOp",EDGE,"E84.left");Q116=makeQuery(id+"F0.imprint","IMPRINT",FACE,{"disambiguationData":[TD([[makeQuery(id+"F0.imprint","IMPRINT",EDGE,{"derivedFrom":subQ3}),-1.0]])]});}
            var Q117;
            {var subQ0=sQuery(id+"F0.wireOp",EDGE,"E69.left");Q117=makeQuery(id+"F0.imprint","IMPRINT",FACE,{"disambiguationData":[TD([[makeQuery(id+"F0.imprint","IMPRINT",EDGE,{"derivedFrom":subQ0}),1.0]])]});}
            var Q118;
            {var subQ0=sQuery(id+"F0.wireOp",EDGE,"E71.left");Q118=makeQuery(id+"F0.imprint","IMPRINT",FACE,{"disambiguationData":[TD([[makeQuery(id+"F0.imprint","IMPRINT",EDGE,{"derivedFrom":subQ0}),1.0]])]});}
            var Q119;
            {var subQ0=sQuery(id+"F0.wireOp",EDGE,"E77.left");Q119=makeQuery(id+"F0.imprint","IMPRINT",FACE,{"disambiguationData":[TD([[makeQuery(id+"F0.imprint","IMPRINT",EDGE,{"derivedFrom":subQ0}),1.0]])]});}
            var Q120;
            {var subQ3=sQuery(id+"F0.wireOp",EDGE,"E61.right");Q120=makeQuery(id+"F0.imprint","IMPRINT",FACE,{"disambiguationData":[TD([[makeQuery(id+"F0.imprint","IMPRINT",EDGE,{"derivedFrom":subQ3}),1.0]])]});}
            var Q121;
            {var subQ0=sQuery(id+"F0.wireOp",EDGE,"E267.left");Q121=makeQuery(id+"F0.imprint","IMPRINT",FACE,{"disambiguationData":[TD([[makeQuery(id+"F0.imprint","IMPRINT",EDGE,{"derivedFrom":subQ0}),-1.0]])]});}
            var Q122;
            {var subQ0=sQuery(id+"F0.wireOp",EDGE,"E270.left");Q122=makeQuery(id+"F0.imprint","IMPRINT",FACE,{"disambiguationData":[TD([[makeQuery(id+"F0.imprint","IMPRINT",EDGE,{"derivedFrom":subQ0}),-1.0]])]});}
            var Q123;
            {var subQ0=sQuery(id+"F0.wireOp",EDGE,"E272.left");Q123=makeQuery(id+"F0.imprint","IMPRINT",FACE,{"disambiguationData":[TD([[makeQuery(id+"F0.imprint","IMPRINT",EDGE,{"derivedFrom":subQ0}),-1.0]])]});}
            var Q124;
            {var subQ4=sQuery(id+"F0.wireOp",EDGE,"E271.left");Q124=makeQuery(id+"F0.imprint","IMPRINT",FACE,{"disambiguationData":[TD([[makeQuery(id+"F0.imprint","IMPRINT",EDGE,{"derivedFrom":subQ4}),-1.0]])]});}
            var Q125;
            {var subQ0=sQuery(id+"F0.wireOp",EDGE,"E264.right");Q125=makeQuery(id+"F0.imprint","IMPRINT",FACE,{"disambiguationData":[TD([[makeQuery(id+"F0.imprint","IMPRINT",EDGE,{"derivedFrom":subQ0}),1.0]])]});}
            var Q126;
            {var subQ0=sQuery(id+"F0.wireOp",EDGE,"E263.right");Q126=makeQuery(id+"F0.imprint","IMPRINT",FACE,{"disambiguationData":[TD([[makeQuery(id+"F0.imprint","IMPRINT",EDGE,{"derivedFrom":subQ0}),1.0]])]});}
            var Q127;
            {var subQ2=sQuery(id+"F0.wireOp",EDGE,"E266.left");Q127=makeQuery(id+"F0.imprint","IMPRINT",FACE,{"disambiguationData":[TD([[makeQuery(id+"F0.imprint","IMPRINT",EDGE,{"derivedFrom":subQ2}),-1.0]])]});}
            var Q128;
            {var subQ0=sQuery(id+"F0.wireOp",EDGE,"E269.left");Q128=makeQuery(id+"F0.imprint","IMPRINT",FACE,{"disambiguationData":[TD([[makeQuery(id+"F0.imprint","IMPRINT",EDGE,{"derivedFrom":subQ0}),1.0]])]});}
            var Q129;
            {var subQ0=sQuery(id+"F0.wireOp",EDGE,"E270.left");Q129=makeQuery(id+"F0.imprint","IMPRINT",FACE,{"disambiguationData":[TD([[makeQuery(id+"F0.imprint","IMPRINT",EDGE,{"derivedFrom":subQ0}),1.0]])]});}
            var Q130;
            {var subQ0=sQuery(id+"F0.wireOp",EDGE,"E268.left");Q130=makeQuery(id+"F0.imprint","IMPRINT",FACE,{"disambiguationData":[TD([[makeQuery(id+"F0.imprint","IMPRINT",EDGE,{"derivedFrom":subQ0}),1.0]])]});}
            var Q131;
            {var subQ3=sQuery(id+"F0.wireOp",EDGE,"E267.right");Q131=makeQuery(id+"F0.imprint","IMPRINT",FACE,{"disambiguationData":[TD([[makeQuery(id+"F0.imprint","IMPRINT",EDGE,{"derivedFrom":subQ3}),1.0]])]});}
            var Q132;
            {var subQ0=sQuery(id+"F0.wireOp",EDGE,"E272.left");Q132=makeQuery(id+"F0.imprint","IMPRINT",FACE,{"disambiguationData":[TD([[makeQuery(id+"F0.imprint","IMPRINT",EDGE,{"derivedFrom":subQ0}),1.0]])]});}
            var Q133;
            {var subQ0=sQuery(id+"F0.wireOp",EDGE,"E271.left");Q133=makeQuery(id+"F0.imprint","IMPRINT",FACE,{"disambiguationData":[TD([[makeQuery(id+"F0.imprint","IMPRINT",EDGE,{"derivedFrom":subQ0}),1.0]])]});}
            var Q134;
            {var subQ0=sQuery(id+"F0.wireOp",EDGE,"E273.left");Q134=makeQuery(id+"F0.imprint","IMPRINT",FACE,{"disambiguationData":[TD([[makeQuery(id+"F0.imprint","IMPRINT",EDGE,{"derivedFrom":subQ0}),1.0]])]});}
            var Q135;
            {var subQ0=sQuery(id+"F0.wireOp",EDGE,"E266.right");Q135=makeQuery(id+"F0.imprint","IMPRINT",FACE,{"disambiguationData":[TD([[makeQuery(id+"F0.imprint","IMPRINT",EDGE,{"derivedFrom":subQ0}),1.0]])]});}
            var Q136;
            {var subQ4=sQuery(id+"F0.wireOp",EDGE,"E265.right");Q136=makeQuery(id+"F0.imprint","IMPRINT",FACE,{"disambiguationData":[TD([[makeQuery(id+"F0.imprint","IMPRINT",EDGE,{"derivedFrom":subQ4}),1.0]])]});}
            var Q137;
            {var subQ4=sQuery(id+"F0.wireOp",EDGE,"E275.left");Q137=makeQuery(id+"F0.imprint","IMPRINT",FACE,{"disambiguationData":[TD([[makeQuery(id+"F0.imprint","IMPRINT",EDGE,{"derivedFrom":subQ4}),-1.0]])]});}
            var Q138;
            {var subQ2=sQuery(id+"F0.wireOp",EDGE,"E281.left");Q138=makeQuery(id+"F0.imprint","IMPRINT",FACE,{"disambiguationData":[TD([[makeQuery(id+"F0.imprint","IMPRINT",EDGE,{"derivedFrom":subQ2}),1.0]])]});}
            var Q139;
            {var subQ4=sQuery(id+"F0.wireOp",EDGE,"E276.left");Q139=makeQuery(id+"F0.imprint","IMPRINT",FACE,{"disambiguationData":[TD([[makeQuery(id+"F0.imprint","IMPRINT",EDGE,{"derivedFrom":subQ4}),-1.0]])]});}
            var Q140;
            {var subQ5=sQuery(id+"F0.wireOp",EDGE,"E278.top");Q140=makeQuery(id+"F0.imprint","IMPRINT",FACE,{"disambiguationData":[TD([[makeQuery(id+"F0.imprint","IMPRINT",EDGE,{"derivedFrom":subQ5}),-1.0]])]});}
            var Q141;
            {var subQ0=sQuery(id+"F0.wireOp",EDGE,"E278.bottom");Q141=makeQuery(id+"F0.imprint","IMPRINT",FACE,{"disambiguationData":[TD([[makeQuery(id+"F0.imprint","IMPRINT",EDGE,{"derivedFrom":subQ0}),-1.0]])]});}
            var Q142;
            {var subQ0=sQuery(id+"F0.wireOp",EDGE,"E274.bottom");Q142=makeQuery(id+"F0.imprint","IMPRINT",FACE,{"disambiguationData":[TD([[makeQuery(id+"F0.imprint","IMPRINT",EDGE,{"derivedFrom":subQ0}),-1.0]])]});}
            var Q143;
            {var subQ0=sQuery(id+"F0.wireOp",EDGE,"E277.left");Q143=makeQuery(id+"F0.imprint","IMPRINT",FACE,{"disambiguationData":[TD([[makeQuery(id+"F0.imprint","IMPRINT",EDGE,{"derivedFrom":subQ0}),1.0]])]});}
            var Q144;
            {var subQ5=sQuery(id+"F0.wireOp",EDGE,"E138.right");Q144=makeQuery(id+"F0.imprint","IMPRINT",FACE,{"disambiguationData":[TD([[makeQuery(id+"F0.imprint","IMPRINT",EDGE,{"derivedFrom":subQ5}),1.0]])]});}
            var Q145;
            {var subQ2=sQuery(id+"F0.wireOp",EDGE,"E275.left");Q145=makeQuery(id+"F0.imprint","IMPRINT",FACE,{"disambiguationData":[TD([[makeQuery(id+"F0.imprint","IMPRINT",EDGE,{"derivedFrom":subQ2}),1.0]])]});}
            var Q146;
            Q146=makeQuery(id+"F0.imprint","IMPRINT",FACE,{"disambiguationData":[TD([[makeQuery(id+"F0.imprint","IMPRINT",EDGE,{"derivedFrom":sQuery(id+"F0.wireOp",EDGE,"E174")}),1.0]])]});
            var Q147;
            {var subQ0=sQuery(id+"F0.wireOp",EDGE,"E279.left");Q147=makeQuery(id+"F0.imprint","IMPRINT",FACE,{"disambiguationData":[TD([[makeQuery(id+"F0.imprint","IMPRINT",EDGE,{"derivedFrom":subQ0}),1.0]])]});}
            var Q148;
            {var subQ4=sQuery(id+"F0.wireOp",EDGE,"E138.left");Q148=makeQuery(id+"F0.imprint","IMPRINT",FACE,{"disambiguationData":[TD([[makeQuery(id+"F0.imprint","IMPRINT",EDGE,{"derivedFrom":subQ4}),-1.0]])]});}
            var Q149;
            {var subQ0=sQuery(id+"F0.wireOp",EDGE,"E280.left");Q149=makeQuery(id+"F0.imprint","IMPRINT",FACE,{"disambiguationData":[TD([[makeQuery(id+"F0.imprint","IMPRINT",EDGE,{"derivedFrom":subQ0}),1.0]])]});}
            var Q150;
            {var subQ0=sQuery(id+"F0.wireOp",EDGE,"E276.left");Q150=makeQuery(id+"F0.imprint","IMPRINT",FACE,{"disambiguationData":[TD([[makeQuery(id+"F0.imprint","IMPRINT",EDGE,{"derivedFrom":subQ0}),1.0]])]});}
            var Q151;
            {var subQ0=sQuery(id+"F0.wireOp",EDGE,"E274.top");Q151=makeQuery(id+"F0.imprint","IMPRINT",FACE,{"disambiguationData":[TD([[makeQuery(id+"F0.imprint","IMPRINT",EDGE,{"derivedFrom":subQ0}),-1.0]])]});}
            var Q152;
            {var subQ2=sQuery(id+"F0.wireOp",EDGE,"E282.bottom");Q152=makeQuery(id+"F0.imprint","IMPRINT",FACE,{"disambiguationData":[TD([[makeQuery(id+"F0.imprint","IMPRINT",EDGE,{"derivedFrom":subQ2}),-1.0]])]});}
            var Q153;
            {var subQ9=sQuery(id+"F0.wireOp",EDGE,"E278.bottom");Q153=makeQuery(id+"F0.imprint","IMPRINT",FACE,{"disambiguationData":[TD([[makeQuery(id+"F0.imprint","IMPRINT",EDGE,{"derivedFrom":subQ9}),1.0]])]});}
            var Q154;
            {var subQ2=sQuery(id+"F0.wireOp",EDGE,"E283.bottom");Q154=makeQuery(id+"F0.imprint","IMPRINT",FACE,{"disambiguationData":[TD([[makeQuery(id+"F0.imprint","IMPRINT",EDGE,{"derivedFrom":subQ2}),-1.0]])]});}
            var Q155;
            {var subQ8=sQuery(id+"F0.wireOp",EDGE,"E49.left");Q155=makeQuery(id+"F0.imprint","IMPRINT",FACE,{"disambiguationData":[TD([[makeQuery(id+"F0.imprint","IMPRINT",EDGE,{"derivedFrom":subQ8}),1.0]])]});}
            var Q156;
            {var subQ7=sQuery(id+"F0.wireOp",EDGE,"E248.trimOffspring");Q156=makeQuery(id+"F0.imprint","IMPRINT",FACE,{"disambiguationData":[TD([[makeQuery(id+"F0.imprint","IMPRINT",EDGE,{"derivedFrom":subQ7}),1.0]])]});}
            var Q157;
            {var subQ2=sQuery(id+"F0.wireOp",EDGE,"E284.bottom");Q157=makeQuery(id+"F0.imprint","IMPRINT",FACE,{"disambiguationData":[TD([[makeQuery(id+"F0.imprint","IMPRINT",EDGE,{"derivedFrom":subQ2}),-1.0]])]});}
            var Q158;
            {var subQ2=sQuery(id+"F0.wireOp",EDGE,"E285.bottom");Q158=makeQuery(id+"F0.imprint","IMPRINT",FACE,{"disambiguationData":[TD([[makeQuery(id+"F0.imprint","IMPRINT",EDGE,{"derivedFrom":subQ2}),-1.0]])]});}
            extrude(context, id + "F2", {"entities" : qUnion([Q0, Q1, Q2, Q3, Q4, Q5, Q6, Q7, Q8, Q9, Q10, Q11, Q12, Q13, Q14, Q15, Q16, Q17, Q18, Q19, Q20, Q21, Q22, Q23, Q24, Q25, Q26, Q27, Q28, Q29, Q30, Q31, Q32, Q33, Q34, Q35, Q36, Q37, Q38, Q39, Q40, Q41, Q42, Q43, Q44, Q45, Q46, Q47, Q48, Q49, Q50, Q51, Q52, Q53, Q54, Q55, Q56, Q57, Q58, Q59, Q60, Q61, Q62, Q63, Q64, Q65, Q66, Q67, Q68, Q69, Q70, Q71, Q72, Q73, Q74, Q75, Q76, Q77, Q78, Q79, Q80, Q81, Q82, Q83, Q84, Q85, Q86, Q87, Q88, Q89, Q90, Q91, Q92, Q93, Q94, Q95, Q96, Q97, Q98, Q99, Q100, Q101, Q102, Q103, Q104, Q105, Q106, Q107, Q108, Q109, Q110, Q111, Q112, Q113, Q114, Q115, Q116, Q117, Q118, Q119, Q120, Q121, Q122, Q123, Q124, Q125, Q126, Q127, Q128, Q129, Q130, Q131, Q132, Q133, Q134, Q135, Q136, Q137, Q138, Q139, Q140, Q141, Q142, Q143, Q144, Q145, Q146, Q147, Q148, Q149, Q150, Q151, Q152, Q153, Q154, Q155, Q156, Q157, Q158]), "operationType" : NewBodyOperationType.ADD, "oppositeDirection" : true, "depth" : 12.7 * mm, "offsetDistance" : 25.4 * mm});
        }
        {
            var Q0;
            {var subQ0=sQuery(id+"F0.wireOp",EDGE,"E111.left");Q0=makeQuery(id+"F0.imprint","IMPRINT",FACE,{"disambiguationData":[TD([[makeQuery(id+"F0.imprint","IMPRINT",EDGE,{"derivedFrom":subQ0}),1.0]])]});}
            var Q1;
            {var subQ2=sQuery(id+"F0.wireOp",EDGE,"E67.left");Q1=makeQuery(id+"F0.imprint","IMPRINT",FACE,{"disambiguationData":[TD([[makeQuery(id+"F0.imprint","IMPRINT",EDGE,{"derivedFrom":subQ2}),1.0]])]});}
            var Q2;
            {var subQ0=sQuery(id+"F0.wireOp",EDGE,"E63.left");Q2=makeQuery(id+"F0.imprint","IMPRINT",FACE,{"disambiguationData":[TD([[makeQuery(id+"F0.imprint","IMPRINT",EDGE,{"derivedFrom":subQ0}),1.0]])]});}
            var Q3;
            Q3=makeQuery(id+"F0.imprint","IMPRINT",FACE,{"disambiguationData":[TD([[makeQuery(id+"F0.imprint","IMPRINT",EDGE,{"derivedFrom":sQuery(id+"F0.wireOp",EDGE,"E79.bottom")}),-1.0]])]});
            var Q4;
            Q4=makeQuery(id+"F0.imprint","IMPRINT",FACE,{"disambiguationData":[TD([[makeQuery(id+"F0.imprint","IMPRINT",EDGE,{"derivedFrom":sQuery(id+"F0.wireOp",EDGE,"E118.bottom")}),-1.0]])]});
            var Q5;
            {var subQ0=sQuery(id+"F0.wireOp",EDGE,"E65.left");Q5=makeQuery(id+"F0.imprint","IMPRINT",FACE,{"disambiguationData":[TD([[makeQuery(id+"F0.imprint","IMPRINT",EDGE,{"derivedFrom":subQ0}),1.0]])]});}
            var Q6;
            {var subQ0=sQuery(id+"F0.wireOp",EDGE,"E61.left");Q6=makeQuery(id+"F0.imprint","IMPRINT",FACE,{"disambiguationData":[TD([[makeQuery(id+"F0.imprint","IMPRINT",EDGE,{"derivedFrom":subQ0}),1.0]])]});}
            var Q7;
            {var subQ0=sQuery(id+"F0.wireOp",EDGE,"E69.left");Q7=makeQuery(id+"F0.imprint","IMPRINT",FACE,{"disambiguationData":[TD([[makeQuery(id+"F0.imprint","IMPRINT",EDGE,{"derivedFrom":subQ0}),1.0]])]});}
            var Q8;
            {var subQ0=sQuery(id+"F0.wireOp",EDGE,"E71.left");Q8=makeQuery(id+"F0.imprint","IMPRINT",FACE,{"disambiguationData":[TD([[makeQuery(id+"F0.imprint","IMPRINT",EDGE,{"derivedFrom":subQ0}),1.0]])]});}
            var Q9;
            Q9=makeQuery(id+"F0.imprint","IMPRINT",FACE,{"disambiguationData":[TD([[makeQuery(id+"F0.imprint","IMPRINT",EDGE,{"derivedFrom":sQuery(id+"F0.wireOp",EDGE,"E107.bottom")}),-1.0]])]});
            var Q10;
            Q10=makeQuery(id+"F0.imprint","IMPRINT",FACE,{"disambiguationData":[TD([[makeQuery(id+"F0.imprint","IMPRINT",EDGE,{"derivedFrom":sQuery(id+"F0.wireOp",EDGE,"E103.bottom")}),-1.0]])]});
            var Q11;
            Q11=makeQuery(id+"F0.imprint","IMPRINT",FACE,{"disambiguationData":[TD([[makeQuery(id+"F0.imprint","IMPRINT",EDGE,{"derivedFrom":sQuery(id+"F0.wireOp",EDGE,"E114.bottom")}),-1.0]])]});
            var Q12;
            {var subQ0=sQuery(id+"F0.wireOp",EDGE,"E73.left");Q12=makeQuery(id+"F0.imprint","IMPRINT",FACE,{"disambiguationData":[TD([[makeQuery(id+"F0.imprint","IMPRINT",EDGE,{"derivedFrom":subQ0}),1.0]])]});}
            var Q13;
            {var subQ0=sQuery(id+"F0.wireOp",EDGE,"E75.left");Q13=makeQuery(id+"F0.imprint","IMPRINT",FACE,{"disambiguationData":[TD([[makeQuery(id+"F0.imprint","IMPRINT",EDGE,{"derivedFrom":subQ0}),1.0]])]});}
            var Q14;
            {var subQ0=sQuery(id+"F0.wireOp",EDGE,"E77.left");Q14=makeQuery(id+"F0.imprint","IMPRINT",FACE,{"disambiguationData":[TD([[makeQuery(id+"F0.imprint","IMPRINT",EDGE,{"derivedFrom":subQ0}),1.0]])]});}
            var Q15;
            {var subQ0=sQuery(id+"F0.wireOp",EDGE,"E86.left");Q15=makeQuery(id+"F0.imprint","IMPRINT",FACE,{"disambiguationData":[TD([[makeQuery(id+"F0.imprint","IMPRINT",EDGE,{"derivedFrom":subQ0}),1.0]])]});}
            var Q16;
            {var subQ2=sQuery(id+"F0.wireOp",EDGE,"E84.left");Q16=makeQuery(id+"F0.imprint","IMPRINT",FACE,{"disambiguationData":[TD([[makeQuery(id+"F0.imprint","IMPRINT",EDGE,{"derivedFrom":subQ2}),1.0]])]});}
            var Q17;
            {var subQ0=sQuery(id+"F0.wireOp",EDGE,"E82.left");Q17=makeQuery(id+"F0.imprint","IMPRINT",FACE,{"disambiguationData":[TD([[makeQuery(id+"F0.imprint","IMPRINT",EDGE,{"derivedFrom":subQ0}),1.0]])]});}
            var Q18;
            {var subQ0=sQuery(id+"F0.wireOp",EDGE,"E154.left");Q18=makeQuery(id+"F0.imprint","IMPRINT",FACE,{"disambiguationData":[TD([[makeQuery(id+"F0.imprint","IMPRINT",EDGE,{"derivedFrom":subQ0}),1.0]])]});}
            var Q19;
            {var subQ0=sQuery(id+"F0.wireOp",EDGE,"E158.left");Q19=makeQuery(id+"F0.imprint","IMPRINT",FACE,{"disambiguationData":[TD([[makeQuery(id+"F0.imprint","IMPRINT",EDGE,{"derivedFrom":subQ0}),1.0]])]});}
            var Q20;
            {var subQ2=sQuery(id+"F0.wireOp",EDGE,"E162.left");Q20=makeQuery(id+"F0.imprint","IMPRINT",FACE,{"disambiguationData":[TD([[makeQuery(id+"F0.imprint","IMPRINT",EDGE,{"derivedFrom":subQ2}),1.0]])]});}
            var Q21;
            {var subQ0=sQuery(id+"F0.wireOp",EDGE,"E166.left");Q21=makeQuery(id+"F0.imprint","IMPRINT",FACE,{"disambiguationData":[TD([[makeQuery(id+"F0.imprint","IMPRINT",EDGE,{"derivedFrom":subQ0}),1.0]])]});}
            var Q22;
            {var subQ2=sQuery(id+"F0.wireOp",EDGE,"E234.left");Q22=makeQuery(id+"F0.imprint","IMPRINT",FACE,{"disambiguationData":[TD([[makeQuery(id+"F0.imprint","IMPRINT",EDGE,{"derivedFrom":subQ2}),1.0]])]});}
            var Q23;
            {var subQ0=sQuery(id+"F0.wireOp",EDGE,"E231.left");Q23=makeQuery(id+"F0.imprint","IMPRINT",FACE,{"disambiguationData":[TD([[makeQuery(id+"F0.imprint","IMPRINT",EDGE,{"derivedFrom":subQ0}),1.0]])]});}
            var Q24;
            {var subQ0=sQuery(id+"F0.wireOp",EDGE,"E213.left");Q24=makeQuery(id+"F0.imprint","IMPRINT",FACE,{"disambiguationData":[TD([[makeQuery(id+"F0.imprint","IMPRINT",EDGE,{"derivedFrom":subQ0}),1.0]])]});}
            var Q25;
            {var subQ2=sQuery(id+"F0.wireOp",EDGE,"E215.left");Q25=makeQuery(id+"F0.imprint","IMPRINT",FACE,{"disambiguationData":[TD([[makeQuery(id+"F0.imprint","IMPRINT",EDGE,{"derivedFrom":subQ2}),1.0]])]});}
            var Q26;
            {var subQ2=sQuery(id+"F0.wireOp",EDGE,"E202.left");Q26=makeQuery(id+"F0.imprint","IMPRINT",FACE,{"disambiguationData":[TD([[makeQuery(id+"F0.imprint","IMPRINT",EDGE,{"derivedFrom":subQ2}),1.0]])]});}
            var Q27;
            {var subQ2=sQuery(id+"F0.wireOp",EDGE,"E204.left");Q27=makeQuery(id+"F0.imprint","IMPRINT",FACE,{"disambiguationData":[TD([[makeQuery(id+"F0.imprint","IMPRINT",EDGE,{"derivedFrom":subQ2}),1.0]])]});}
            var Q28;
            {var subQ2=sQuery(id+"F0.wireOp",EDGE,"E221.left");Q28=makeQuery(id+"F0.imprint","IMPRINT",FACE,{"disambiguationData":[TD([[makeQuery(id+"F0.imprint","IMPRINT",EDGE,{"derivedFrom":subQ2}),1.0]])]});}
            var Q29;
            {var subQ2=sQuery(id+"F0.wireOp",EDGE,"E223.left");Q29=makeQuery(id+"F0.imprint","IMPRINT",FACE,{"disambiguationData":[TD([[makeQuery(id+"F0.imprint","IMPRINT",EDGE,{"derivedFrom":subQ2}),1.0]])]});}
            var Q30;
            {var subQ0=sQuery(id+"F0.wireOp",EDGE,"E228.left");Q30=makeQuery(id+"F0.imprint","IMPRINT",FACE,{"disambiguationData":[TD([[makeQuery(id+"F0.imprint","IMPRINT",EDGE,{"derivedFrom":subQ0}),1.0]])]});}
            extrude(context, id + "F3", {"entities" : qUnion([Q0, Q1, Q2, Q3, Q4, Q5, Q6, Q7, Q8, Q9, Q10, Q11, Q12, Q13, Q14, Q15, Q16, Q17, Q18, Q19, Q20, Q21, Q22, Q23, Q24, Q25, Q26, Q27, Q28, Q29, Q30]), "operationType" : NewBodyOperationType.REMOVE, "depth" : 2286 * mm, "offsetDistance" : 25.4 * mm});
        }
        {
            var Q0;
            {var subQ0=sQuery(id+"F0.wireOp",EDGE,"E77.left");Q0=makeQuery(id+"F0.imprint","IMPRINT",FACE,{"disambiguationData":[TD([[makeQuery(id+"F0.imprint","IMPRINT",EDGE,{"derivedFrom":subQ0}),1.0]])]});}
            var Q1;
            {var subQ0=sQuery(id+"F0.wireOp",EDGE,"E75.left");Q1=makeQuery(id+"F0.imprint","IMPRINT",FACE,{"disambiguationData":[TD([[makeQuery(id+"F0.imprint","IMPRINT",EDGE,{"derivedFrom":subQ0}),1.0]])]});}
            var Q2;
            {var subQ0=sQuery(id+"F0.wireOp",EDGE,"E73.left");Q2=makeQuery(id+"F0.imprint","IMPRINT",FACE,{"disambiguationData":[TD([[makeQuery(id+"F0.imprint","IMPRINT",EDGE,{"derivedFrom":subQ0}),1.0]])]});}
            var Q3;
            {var subQ0=sQuery(id+"F0.wireOp",EDGE,"E71.left");Q3=makeQuery(id+"F0.imprint","IMPRINT",FACE,{"disambiguationData":[TD([[makeQuery(id+"F0.imprint","IMPRINT",EDGE,{"derivedFrom":subQ0}),1.0]])]});}
            var Q4;
            {var subQ0=sQuery(id+"F0.wireOp",EDGE,"E69.left");Q4=makeQuery(id+"F0.imprint","IMPRINT",FACE,{"disambiguationData":[TD([[makeQuery(id+"F0.imprint","IMPRINT",EDGE,{"derivedFrom":subQ0}),1.0]])]});}
            var Q5;
            {var subQ0=sQuery(id+"F0.wireOp",EDGE,"E61.left");Q5=makeQuery(id+"F0.imprint","IMPRINT",FACE,{"disambiguationData":[TD([[makeQuery(id+"F0.imprint","IMPRINT",EDGE,{"derivedFrom":subQ0}),1.0]])]});}
            var Q6;
            {var subQ0=sQuery(id+"F0.wireOp",EDGE,"E65.left");Q6=makeQuery(id+"F0.imprint","IMPRINT",FACE,{"disambiguationData":[TD([[makeQuery(id+"F0.imprint","IMPRINT",EDGE,{"derivedFrom":subQ0}),1.0]])]});}
            var Q7;
            {var subQ0=sQuery(id+"F0.wireOp",EDGE,"E63.left");Q7=makeQuery(id+"F0.imprint","IMPRINT",FACE,{"disambiguationData":[TD([[makeQuery(id+"F0.imprint","IMPRINT",EDGE,{"derivedFrom":subQ0}),1.0]])]});}
            var Q8;
            {var subQ0=sQuery(id+"F0.wireOp",EDGE,"E86.left");Q8=makeQuery(id+"F0.imprint","IMPRINT",FACE,{"disambiguationData":[TD([[makeQuery(id+"F0.imprint","IMPRINT",EDGE,{"derivedFrom":subQ0}),1.0]])]});}
            var Q9;
            {var subQ2=sQuery(id+"F0.wireOp",EDGE,"E84.left");Q9=makeQuery(id+"F0.imprint","IMPRINT",FACE,{"disambiguationData":[TD([[makeQuery(id+"F0.imprint","IMPRINT",EDGE,{"derivedFrom":subQ2}),1.0]])]});}
            var Q10;
            {var subQ0=sQuery(id+"F0.wireOp",EDGE,"E82.left");Q10=makeQuery(id+"F0.imprint","IMPRINT",FACE,{"disambiguationData":[TD([[makeQuery(id+"F0.imprint","IMPRINT",EDGE,{"derivedFrom":subQ0}),1.0]])]});}
            var Q11;
            {var subQ2=sQuery(id+"F0.wireOp",EDGE,"E67.left");Q11=makeQuery(id+"F0.imprint","IMPRINT",FACE,{"disambiguationData":[TD([[makeQuery(id+"F0.imprint","IMPRINT",EDGE,{"derivedFrom":subQ2}),1.0]])]});}
            var Q12;
            {var subQ0=sQuery(id+"F0.wireOp",EDGE,"E111.left");Q12=makeQuery(id+"F0.imprint","IMPRINT",FACE,{"disambiguationData":[TD([[makeQuery(id+"F0.imprint","IMPRINT",EDGE,{"derivedFrom":subQ0}),1.0]])]});}
            var Q13;
            Q13=makeQuery(id+"F0.imprint","IMPRINT",FACE,{"disambiguationData":[TD([[makeQuery(id+"F0.imprint","IMPRINT",EDGE,{"derivedFrom":sQuery(id+"F0.wireOp",EDGE,"E79.bottom")}),-1.0]])]});
            var Q14;
            Q14=makeQuery(id+"F0.imprint","IMPRINT",FACE,{"disambiguationData":[TD([[makeQuery(id+"F0.imprint","IMPRINT",EDGE,{"derivedFrom":sQuery(id+"F0.wireOp",EDGE,"E118.bottom")}),-1.0]])]});
            var Q15;
            Q15=makeQuery(id+"F0.imprint","IMPRINT",FACE,{"disambiguationData":[TD([[makeQuery(id+"F0.imprint","IMPRINT",EDGE,{"derivedFrom":sQuery(id+"F0.wireOp",EDGE,"E107.bottom")}),-1.0]])]});
            var Q16;
            Q16=makeQuery(id+"F0.imprint","IMPRINT",FACE,{"disambiguationData":[TD([[makeQuery(id+"F0.imprint","IMPRINT",EDGE,{"derivedFrom":sQuery(id+"F0.wireOp",EDGE,"E103.bottom")}),-1.0]])]});
            var Q17;
            Q17=makeQuery(id+"F0.imprint","IMPRINT",FACE,{"disambiguationData":[TD([[makeQuery(id+"F0.imprint","IMPRINT",EDGE,{"derivedFrom":sQuery(id+"F0.wireOp",EDGE,"E114.bottom")}),-1.0]])]});
            var Q18;
            {var subQ0=sQuery(id+"F0.wireOp",EDGE,"E166.left");Q18=makeQuery(id+"F0.imprint","IMPRINT",FACE,{"disambiguationData":[TD([[makeQuery(id+"F0.imprint","IMPRINT",EDGE,{"derivedFrom":subQ0}),1.0]])]});}
            var Q19;
            {var subQ2=sQuery(id+"F0.wireOp",EDGE,"E162.left");Q19=makeQuery(id+"F0.imprint","IMPRINT",FACE,{"disambiguationData":[TD([[makeQuery(id+"F0.imprint","IMPRINT",EDGE,{"derivedFrom":subQ2}),1.0]])]});}
            var Q20;
            {var subQ0=sQuery(id+"F0.wireOp",EDGE,"E158.left");Q20=makeQuery(id+"F0.imprint","IMPRINT",FACE,{"disambiguationData":[TD([[makeQuery(id+"F0.imprint","IMPRINT",EDGE,{"derivedFrom":subQ0}),1.0]])]});}
            var Q21;
            {var subQ0=sQuery(id+"F0.wireOp",EDGE,"E154.left");Q21=makeQuery(id+"F0.imprint","IMPRINT",FACE,{"disambiguationData":[TD([[makeQuery(id+"F0.imprint","IMPRINT",EDGE,{"derivedFrom":subQ0}),1.0]])]});}
            var Q22;
            {var subQ2=sQuery(id+"F0.wireOp",EDGE,"E234.left");Q22=makeQuery(id+"F0.imprint","IMPRINT",FACE,{"disambiguationData":[TD([[makeQuery(id+"F0.imprint","IMPRINT",EDGE,{"derivedFrom":subQ2}),1.0]])]});}
            var Q23;
            {var subQ0=sQuery(id+"F0.wireOp",EDGE,"E231.left");Q23=makeQuery(id+"F0.imprint","IMPRINT",FACE,{"disambiguationData":[TD([[makeQuery(id+"F0.imprint","IMPRINT",EDGE,{"derivedFrom":subQ0}),1.0]])]});}
            var Q24;
            {var subQ0=sQuery(id+"F0.wireOp",EDGE,"E213.left");Q24=makeQuery(id+"F0.imprint","IMPRINT",FACE,{"disambiguationData":[TD([[makeQuery(id+"F0.imprint","IMPRINT",EDGE,{"derivedFrom":subQ0}),1.0]])]});}
            var Q25;
            {var subQ2=sQuery(id+"F0.wireOp",EDGE,"E215.left");Q25=makeQuery(id+"F0.imprint","IMPRINT",FACE,{"disambiguationData":[TD([[makeQuery(id+"F0.imprint","IMPRINT",EDGE,{"derivedFrom":subQ2}),1.0]])]});}
            var Q26;
            {var subQ2=sQuery(id+"F0.wireOp",EDGE,"E202.left");Q26=makeQuery(id+"F0.imprint","IMPRINT",FACE,{"disambiguationData":[TD([[makeQuery(id+"F0.imprint","IMPRINT",EDGE,{"derivedFrom":subQ2}),1.0]])]});}
            var Q27;
            {var subQ2=sQuery(id+"F0.wireOp",EDGE,"E204.left");Q27=makeQuery(id+"F0.imprint","IMPRINT",FACE,{"disambiguationData":[TD([[makeQuery(id+"F0.imprint","IMPRINT",EDGE,{"derivedFrom":subQ2}),1.0]])]});}
            var Q28;
            {var subQ2=sQuery(id+"F0.wireOp",EDGE,"E221.left");Q28=makeQuery(id+"F0.imprint","IMPRINT",FACE,{"disambiguationData":[TD([[makeQuery(id+"F0.imprint","IMPRINT",EDGE,{"derivedFrom":subQ2}),1.0]])]});}
            var Q29;
            {var subQ2=sQuery(id+"F0.wireOp",EDGE,"E223.left");Q29=makeQuery(id+"F0.imprint","IMPRINT",FACE,{"disambiguationData":[TD([[makeQuery(id+"F0.imprint","IMPRINT",EDGE,{"derivedFrom":subQ2}),1.0]])]});}
            var Q30;
            {var subQ0=sQuery(id+"F0.wireOp",EDGE,"E228.left");Q30=makeQuery(id+"F0.imprint","IMPRINT",FACE,{"disambiguationData":[TD([[makeQuery(id+"F0.imprint","IMPRINT",EDGE,{"derivedFrom":subQ0}),1.0]])]});}
            extrude(context, id + "F4", {"entities" : qUnion([Q0, Q1, Q2, Q3, Q4, Q5, Q6, Q7, Q8, Q9, Q10, Q11, Q12, Q13, Q14, Q15, Q16, Q17, Q18, Q19, Q20, Q21, Q22, Q23, Q24, Q25, Q26, Q27, Q28, Q29, Q30]), "operationType" : NewBodyOperationType.ADD, "depth" : 457.2 * mm, "offsetDistance" : 25.4 * mm});
        }
        {
            var Q0;
            {var subQ0=sQuery(id+"F0.wireOp",EDGE,"E263.left");Q0=makeQuery(id+"F0.imprint","IMPRINT",FACE,{"disambiguationData":[TD([[makeQuery(id+"F0.imprint","IMPRINT",EDGE,{"derivedFrom":subQ0}),1.0]])]});}
            var Q1;
            {var subQ0=sQuery(id+"F0.wireOp",EDGE,"E264.left");Q1=makeQuery(id+"F0.imprint","IMPRINT",FACE,{"disambiguationData":[TD([[makeQuery(id+"F0.imprint","IMPRINT",EDGE,{"derivedFrom":subQ0}),1.0]])]});}
            var Q2;
            {var subQ0=sQuery(id+"F0.wireOp",EDGE,"E265.left");Q2=makeQuery(id+"F0.imprint","IMPRINT",FACE,{"disambiguationData":[TD([[makeQuery(id+"F0.imprint","IMPRINT",EDGE,{"derivedFrom":subQ0}),1.0]])]});}
            var Q3;
            {var subQ0=sQuery(id+"F0.wireOp",EDGE,"E269.left");Q3=makeQuery(id+"F0.imprint","IMPRINT",FACE,{"disambiguationData":[TD([[makeQuery(id+"F0.imprint","IMPRINT",EDGE,{"derivedFrom":subQ0}),1.0]])]});}
            var Q4;
            {var subQ0=sQuery(id+"F0.wireOp",EDGE,"E267.left");Q4=makeQuery(id+"F0.imprint","IMPRINT",FACE,{"disambiguationData":[TD([[makeQuery(id+"F0.imprint","IMPRINT",EDGE,{"derivedFrom":subQ0}),1.0]])]});}
            var Q5;
            {var subQ0=sQuery(id+"F0.wireOp",EDGE,"E268.left");Q5=makeQuery(id+"F0.imprint","IMPRINT",FACE,{"disambiguationData":[TD([[makeQuery(id+"F0.imprint","IMPRINT",EDGE,{"derivedFrom":subQ0}),1.0]])]});}
            var Q6;
            {var subQ0=sQuery(id+"F0.wireOp",EDGE,"E266.left");Q6=makeQuery(id+"F0.imprint","IMPRINT",FACE,{"disambiguationData":[TD([[makeQuery(id+"F0.imprint","IMPRINT",EDGE,{"derivedFrom":subQ0}),1.0]])]});}
            var Q7;
            {var subQ0=sQuery(id+"F0.wireOp",EDGE,"E273.left");Q7=makeQuery(id+"F0.imprint","IMPRINT",FACE,{"disambiguationData":[TD([[makeQuery(id+"F0.imprint","IMPRINT",EDGE,{"derivedFrom":subQ0}),1.0]])]});}
            var Q8;
            {var subQ0=sQuery(id+"F0.wireOp",EDGE,"E272.left");Q8=makeQuery(id+"F0.imprint","IMPRINT",FACE,{"disambiguationData":[TD([[makeQuery(id+"F0.imprint","IMPRINT",EDGE,{"derivedFrom":subQ0}),1.0]])]});}
            var Q9;
            {var subQ0=sQuery(id+"F0.wireOp",EDGE,"E271.left");Q9=makeQuery(id+"F0.imprint","IMPRINT",FACE,{"disambiguationData":[TD([[makeQuery(id+"F0.imprint","IMPRINT",EDGE,{"derivedFrom":subQ0}),1.0]])]});}
            var Q10;
            {var subQ0=sQuery(id+"F0.wireOp",EDGE,"E270.left");Q10=makeQuery(id+"F0.imprint","IMPRINT",FACE,{"disambiguationData":[TD([[makeQuery(id+"F0.imprint","IMPRINT",EDGE,{"derivedFrom":subQ0}),1.0]])]});}
            var Q11;
            {var subQ0=sQuery(id+"F0.wireOp",EDGE,"E278.bottom");Q11=makeQuery(id+"F0.imprint","IMPRINT",FACE,{"disambiguationData":[TD([[makeQuery(id+"F0.imprint","IMPRINT",EDGE,{"derivedFrom":subQ0}),-1.0]])]});}
            var Q12;
            {var subQ0=sQuery(id+"F0.wireOp",EDGE,"E274.bottom");Q12=makeQuery(id+"F0.imprint","IMPRINT",FACE,{"disambiguationData":[TD([[makeQuery(id+"F0.imprint","IMPRINT",EDGE,{"derivedFrom":subQ0}),-1.0]])]});}
            var Q13;
            {var subQ2=sQuery(id+"F0.wireOp",EDGE,"E275.left");Q13=makeQuery(id+"F0.imprint","IMPRINT",FACE,{"disambiguationData":[TD([[makeQuery(id+"F0.imprint","IMPRINT",EDGE,{"derivedFrom":subQ2}),1.0]])]});}
            var Q14;
            {var subQ0=sQuery(id+"F0.wireOp",EDGE,"E276.left");Q14=makeQuery(id+"F0.imprint","IMPRINT",FACE,{"disambiguationData":[TD([[makeQuery(id+"F0.imprint","IMPRINT",EDGE,{"derivedFrom":subQ0}),1.0]])]});}
            var Q15;
            {var subQ0=sQuery(id+"F0.wireOp",EDGE,"E277.left");Q15=makeQuery(id+"F0.imprint","IMPRINT",FACE,{"disambiguationData":[TD([[makeQuery(id+"F0.imprint","IMPRINT",EDGE,{"derivedFrom":subQ0}),1.0]])]});}
            var Q16;
            {var subQ0=sQuery(id+"F0.wireOp",EDGE,"E279.left");Q16=makeQuery(id+"F0.imprint","IMPRINT",FACE,{"disambiguationData":[TD([[makeQuery(id+"F0.imprint","IMPRINT",EDGE,{"derivedFrom":subQ0}),1.0]])]});}
            var Q17;
            {var subQ0=sQuery(id+"F0.wireOp",EDGE,"E280.left");Q17=makeQuery(id+"F0.imprint","IMPRINT",FACE,{"disambiguationData":[TD([[makeQuery(id+"F0.imprint","IMPRINT",EDGE,{"derivedFrom":subQ0}),1.0]])]});}
            var Q18;
            {var subQ2=sQuery(id+"F0.wireOp",EDGE,"E281.left");Q18=makeQuery(id+"F0.imprint","IMPRINT",FACE,{"disambiguationData":[TD([[makeQuery(id+"F0.imprint","IMPRINT",EDGE,{"derivedFrom":subQ2}),1.0]])]});}
            var Q19;
            {var subQ2=sQuery(id+"F0.wireOp",EDGE,"E282.bottom");Q19=makeQuery(id+"F0.imprint","IMPRINT",FACE,{"disambiguationData":[TD([[makeQuery(id+"F0.imprint","IMPRINT",EDGE,{"derivedFrom":subQ2}),-1.0]])]});}
            var Q20;
            {var subQ2=sQuery(id+"F0.wireOp",EDGE,"E283.bottom");Q20=makeQuery(id+"F0.imprint","IMPRINT",FACE,{"disambiguationData":[TD([[makeQuery(id+"F0.imprint","IMPRINT",EDGE,{"derivedFrom":subQ2}),-1.0]])]});}
            var Q21;
            {var subQ2=sQuery(id+"F0.wireOp",EDGE,"E285.bottom");Q21=makeQuery(id+"F0.imprint","IMPRINT",FACE,{"disambiguationData":[TD([[makeQuery(id+"F0.imprint","IMPRINT",EDGE,{"derivedFrom":subQ2}),-1.0]])]});}
            var Q22;
            {var subQ2=sQuery(id+"F0.wireOp",EDGE,"E284.bottom");Q22=makeQuery(id+"F0.imprint","IMPRINT",FACE,{"disambiguationData":[TD([[makeQuery(id+"F0.imprint","IMPRINT",EDGE,{"derivedFrom":subQ2}),-1.0]])]});}
            extrude(context, id + "F5", {"entities" : qUnion([Q0, Q1, Q2, Q3, Q4, Q5, Q6, Q7, Q8, Q9, Q10, Q11, Q12, Q13, Q14, Q15, Q16, Q17, Q18, Q19, Q20, Q21, Q22]), "operationType" : NewBodyOperationType.REMOVE, "depth" : 2159 * mm, "offsetDistance" : 25.4 * mm});
        }
    });
